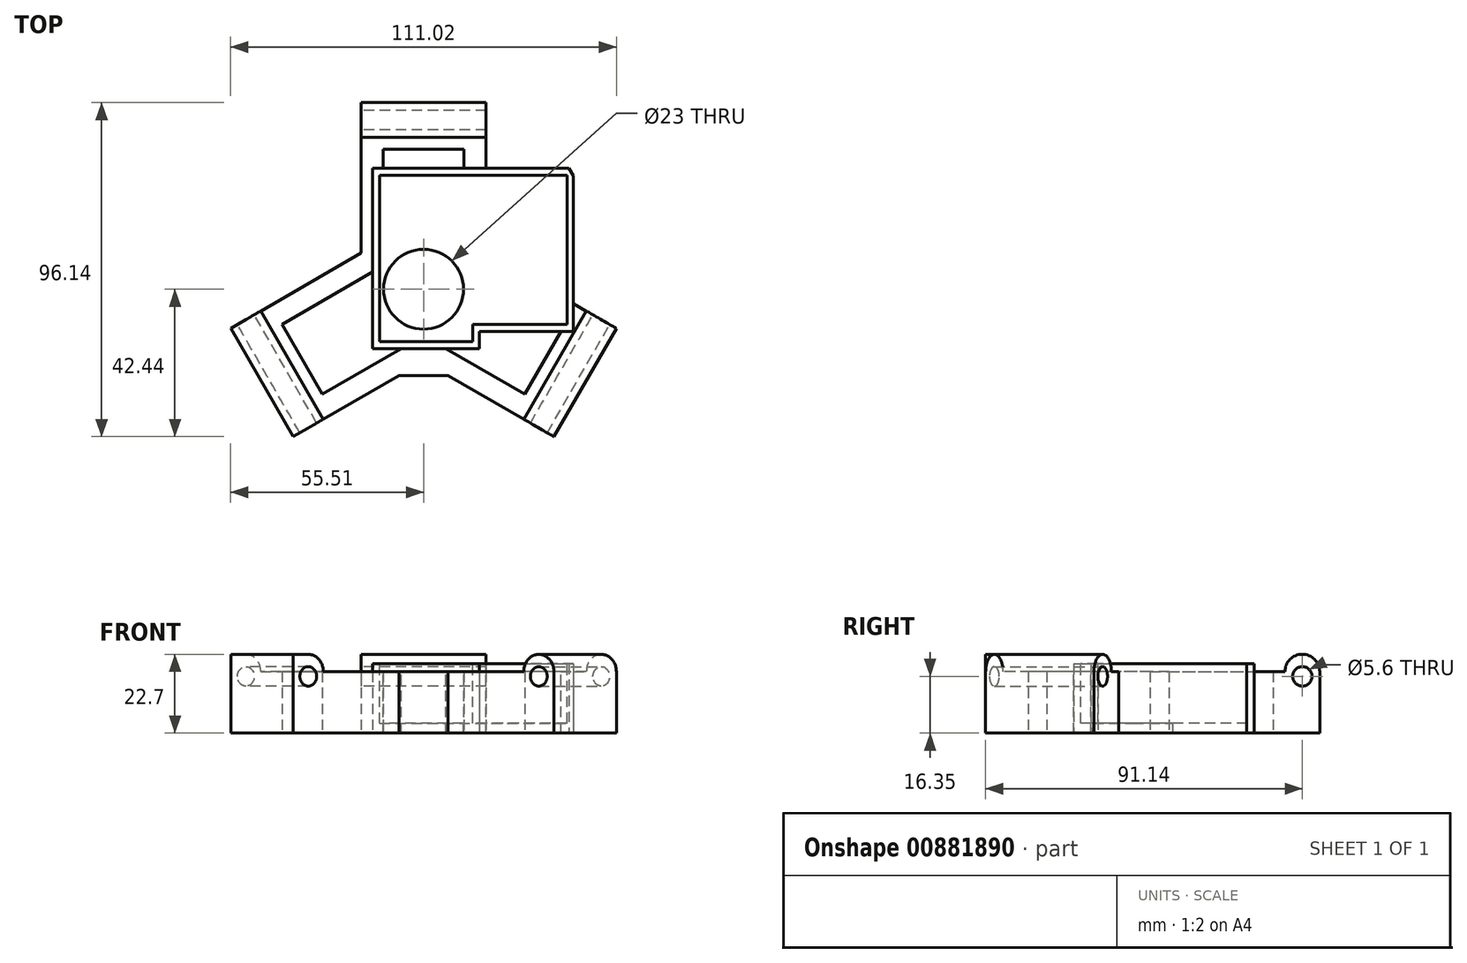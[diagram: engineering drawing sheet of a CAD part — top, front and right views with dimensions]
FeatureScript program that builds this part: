
annotation { "Feature Type Name" : "Feature", "Feature Type Description" : "" }
export const myFeature = defineFeature(function(context is Context, id is Id, definition is map)
    precondition{}
    {
        {
            var Q0;
            Q0=qCreatedBy(makeId("Top.planeOp"),FACE);
            var sketch = newSketch(context, id + "F0", { "sketchPlane" : qUnion([Q0])});
            skCircle(sketch, "E0", {"center": v(0, 0) * mm, "radius": 11.5 * mm});
            skSolve(sketch);
        }
        {
            var Q0;
            Q0=qSketchRegion(id+"F0",true);
            extrude(context, id + "F1", {"entities" : qUnion([Q0]), "depth" : 30.5 * mm, "offsetDistance" : 25 * mm});
        }
        {
            var Q0;
            Q0=makeQuery(id+"F1.opExtrude","CAP_FACE",FACE,{"disambiguationData":[OSD([sQuery(id+"F0.wireOp",EDGE,"E0")])],"isStart":false});
            var sketch = newSketch(context, id + "F2", { "sketchPlane" : qUnion([Q0])});
            skLineSegment(sketch, "E1.bottom", {"start": v(-12.7, 32.85) * mm, "end": v(14.1, 32.85) * mm});
            skLineSegment(sketch, "E1.top", {"start": v(-12.7, -15.1) * mm, "end": v(14.1, -15.1) * mm});
            skLineSegment(sketch, "E1.left", {"start": v(-12.7, 32.85) * mm, "end": v(-12.7, -15.1) * mm});
            skLineSegment(sketch, "E1.right", {"start": v(14.1, 32.85) * mm, "end": v(14.1, -15.1) * mm});
            skSolve(sketch);
        }
        {
            var Q0;
            Q0=qSketchRegion(id+"F2",true);
            extrude(context, id + "F3", {"entities" : qUnion([Q0]), "operationType" : NewBodyOperationType.ADD, "depth" : 44.2 * mm, "offsetDistance" : 25 * mm});
        }
        {
            var Q0;
            Q0=makeQuery(id+"F3.opExtrude","SWEPT_FACE",FACE,{"disambiguationData":[OSD([sQuery(id+"F2.wireOp",EDGE,"E1.right")])]});
            var sketch = newSketch(context, id + "F4", { "sketchPlane" : qUnion([Q0])});
            skLineSegment(sketch, "E2.bottom", {"start": v(32.85, 30.5) * mm, "end": v(-9.15, 30.5) * mm});
            skLineSegment(sketch, "E2.top", {"start": v(32.85, 72.5) * mm, "end": v(-9.15, 72.5) * mm});
            skLineSegment(sketch, "E2.left", {"start": v(32.85, 30.5) * mm, "end": v(32.85, 72.5) * mm});
            skLineSegment(sketch, "E2.right", {"start": v(-9.15, 30.5) * mm, "end": v(-9.15, 72.5) * mm});
            skSolve(sketch);
        }
        {
            var Q0;
            Q0=qSketchRegion(id+"F4",true);
            extrude(context, id + "F5", {"entities" : qUnion([Q0]), "operationType" : NewBodyOperationType.ADD, "depth" : 27.2 * mm, "offsetDistance" : 25 * mm});
        }
        {
            var Q0;
            Q0=qCreatedBy(makeId("Top.planeOp"),FACE);
            var sketch = newSketch(context, id + "F6", { "sketchPlane" : qUnion([Q0])});
            skPoint(sketch, "E3", {"position": v(41.8, 0) * mm});
            skPoint(sketch, "E4", {"position": v(-41.8, 0) * mm});
            skPoint(sketch, "E5", {"position": v(0, 0) * mm});
            skPoint(sketch, "E6", {"position": v(0, -35) * mm});
            skPoint(sketch, "E7", {"position": v(0, 35) * mm});
            skPoint(sketch, "E8", {"position": v(-13, -35) * mm});
            skPoint(sketch, "E9", {"position": v(13, -35) * mm});
            skPoint(sketch, "E10", {"position": v(-13, 35) * mm});
            skPoint(sketch, "E11", {"position": v(13, 35) * mm});
            skLineSegment(sketch, "E12", {"start": v(13, 35) * mm, "end": v(41.8, 35) * mm});
            skLineSegment(sketch, "E13", {"start": v(41.8, 35) * mm, "end": v(41.8, 0) * mm});
            skLineSegment(sketch, "E14", {"start": v(41.8, -35) * mm, "end": v(-41.8, -35) * mm});
            skLineSegment(sketch, "E15", {"start": v(-41.8, 35) * mm, "end": v(-41.8, -35) * mm});
            skLineSegment(sketch, "E16", {"start": v(-41.8, 35) * mm, "end": v(13, 35) * mm});
            skLineSegment(sketch, "E17", {"start": v(41.8, 0) * mm, "end": v(41.8, -35) * mm});
            skLineSegment(sketch, "E18", {"start": v(0, 0) * mm, "end": v(0, 32.21) * mm});
            skSolve(sketch);
        }
        {
            var Q0;
            Q0=qSketchRegion(id+"F6",true);
            extrude(context, id + "F7", {"entities" : qUnion([Q0]), "depth" : 39 * mm, "offsetDistance" : 25 * mm});
        }
        {
            var Q0;
            Q0=makeQuery(id+"F3.opExtrude","CAP_FACE",FACE,{"disambiguationData":[OSD([sQuery(id+"F2.wireOp",EDGE,"E1.bottom"),sQuery(id+"F2.wireOp",EDGE,"E1.top"),sQuery(id+"F2.wireOp",EDGE,"E1.left"),sQuery(id+"F2.wireOp",EDGE,"E1.right")])],"isStart":false});
            var Q1;
            Q1=makeQuery(id+"F5.opExtrude","SWEPT_FACE",FACE,{"disambiguationData":[OSD([sQuery(id+"F4.wireOp",EDGE,"E2.top")])]});
            extrude(context, id + "F8", {"entities" : qUnion([Q0, Q1]), "operationType" : NewBodyOperationType.REMOVE, "oppositeDirection" : true, "depth" : 44.8 * mm, "offsetDistance" : 25 * mm});
        }
        {
            var Q0;
            Q0=makeQuery(id+"F8.boolean.opBoolean","COPY",FACE,{"disambiguationData":[TD([makeQuery(id+"F1.opExtrude","SWEPT_FACE",FACE,{"disambiguationData":[OSD([sQuery(id+"F0.wireOp",EDGE,"E0")])]})])],"derivedFrom":makeQuery(id+"F8.opExtrude","CAP_FACE",FACE,{"disambiguationData":[OSD([sQuery(id+"F2.wireOp",EDGE,"E1.bottom"),sQuery(id+"F2.wireOp",EDGE,"E1.top"),sQuery(id+"F2.wireOp",EDGE,"E1.left"),sQuery(id+"F2.wireOp",EDGE,"E1.right")])],"isStart":false})});
            extrude(context, id + "F9", {"entities" : qUnion([Q0]), "operationType" : NewBodyOperationType.REMOVE, "oppositeDirection" : true, "depth" : 49.1 * mm, "offsetDistance" : 25 * mm});
        }
        {
            var Q0;
            Q0=makeQuery(id+"F7.opExtrude","CAP_FACE",FACE,{"disambiguationData":[OSD([sQuery(id+"F6.wireOp",EDGE,"E12"),sQuery(id+"F6.wireOp",EDGE,"E13"),sQuery(id+"F6.wireOp",EDGE,"E14"),sQuery(id+"F6.wireOp",EDGE,"E15"),sQuery(id+"F6.wireOp",EDGE,"E16"),sQuery(id+"F6.wireOp",EDGE,"E17")])],"isStart":true});
            extrude(context, id + "F10", {"entities" : qUnion([Q0]), "operationType" : NewBodyOperationType.REMOVE, "oppositeDirection" : true, "depth" : 25 * mm, "offsetDistance" : 25 * mm});
        }
        {
            var Q0;
            Q0=makeQuery(id+"F8.boolean.opBoolean","COPY",FACE,{"derivedFrom":makeQuery(id+"F8.opExtrude","CAP_FACE",FACE,{"disambiguationData":[OSD([sQuery(id+"F4.wireOp",EDGE,"E2.top")])],"isStart":false})});
            extrude(context, id + "F11", {"entities" : qUnion([Q0]), "operationType" : NewBodyOperationType.ADD, "depth" : 2.2 * mm, "offsetDistance" : 25 * mm});
        }
        {
            var Q0;
            Q0=makeQuery(id+"F8.boolean.opBoolean","COPY",FACE,{"derivedFrom":makeQuery(id+"F8.opExtrude","SWEPT_FACE",FACE,{"disambiguationData":[OSD([sQuery(id+"F2.wireOp",EDGE,"E1.left")])]})});
            extrude(context, id + "F12", {"entities" : qUnion([Q0]), "operationType" : NewBodyOperationType.REMOVE, "oppositeDirection" : true, "depth" : 2 * mm, "offsetDistance" : 25 * mm});
        }
        {
            var Q0;
            Q0=makeQuery(id+"F7.opExtrude","CAP_FACE",FACE,{"disambiguationData":[OSD([sQuery(id+"F6.wireOp",EDGE,"E12"),sQuery(id+"F6.wireOp",EDGE,"E13"),sQuery(id+"F6.wireOp",EDGE,"E14"),sQuery(id+"F6.wireOp",EDGE,"E15"),sQuery(id+"F6.wireOp",EDGE,"E16"),sQuery(id+"F6.wireOp",EDGE,"E17")])],"isStart":false});
            var sketch = newSketch(context, id + "F13", { "sketchPlane" : qUnion([Q0])});
            skCircle(sketch, "E19.cCircle", {"center": v(0, 0) * mm, "radius": 53.7 * mm, "construction": true});
            skLineSegment(sketch, "E19.0", {"start": v(31, -53.7) * mm, "end": v(-31, -53.7) * mm});
            skLineSegment(sketch, "E19.1", {"start": v(-31, -53.7) * mm, "end": v(-62, 0) * mm});
            skLineSegment(sketch, "E19.2", {"start": v(-62, 0) * mm, "end": v(-31, 53.7) * mm});
            skLineSegment(sketch, "E19.3", {"start": v(-31, 53.7) * mm, "end": v(31, 53.7) * mm});
            skLineSegment(sketch, "E19.4", {"start": v(31, 53.7) * mm, "end": v(62, 0) * mm});
            skLineSegment(sketch, "E19.5", {"start": v(62, 0) * mm, "end": v(31, -53.7) * mm});
            skPoint(sketch, "E19.0.midPoint", {"position": v(0, -53.7) * mm});
            skPoint(sketch, "E20", {"position": v(-41.8, -35) * mm});
            skPoint(sketch, "E21", {"position": v(41.8, -35) * mm});
            skPoint(sketch, "E22", {"position": v(-41.8, 35) * mm});
            skPoint(sketch, "E23", {"position": v(41.8, 35) * mm});
            skSolve(sketch);
        }
        {
            var Q0;
            {var subQ2=sQuery(id+"F13.wireOp",EDGE,"E19.3");Q0=makeQuery(id+"F13.imprint","IMPRINT",FACE,{"disambiguationData":[TD([[makeQuery(id+"F13.imprint","IMPRINT",EDGE,{"derivedFrom":subQ2}),-1.0]])]});}
            var Q1;
            {var subQ1=makeQuery(id+"F7.opExtrude","CAP_EDGE",EDGE,{"disambiguationData":[OSD([sQuery(id+"F6.wireOp",EDGE,"E15")])],"isStart":false});Q1=makeQuery(id+"F13.imprint","IMPRINT",FACE,{"disambiguationData":[TD([[makeQuery(id+"F13.imprint","IMPRINT",EDGE,{"derivedFrom":subQ1}),-1.0]])]});}
            var Q2;
            {var subQ0=sQuery(id+"F13.wireOp",EDGE,"E19.0");Q2=makeQuery(id+"F13.imprint","IMPRINT",FACE,{"disambiguationData":[TD([[makeQuery(id+"F13.imprint","IMPRINT",EDGE,{"derivedFrom":subQ0}),-1.0]])]});}
            var Q3;
            {var subQ1=makeQuery(id+"F7.opExtrude","CAP_EDGE",EDGE,{"disambiguationData":[OSD([sQuery(id+"F6.wireOp",EDGE,"E13"),sQuery(id+"F6.wireOp",EDGE,"E17")])],"isStart":false});Q3=makeQuery(id+"F13.imprint","IMPRINT",FACE,{"disambiguationData":[TD([[makeQuery(id+"F13.imprint","IMPRINT",EDGE,{"derivedFrom":subQ1}),1.0]])]});}
            extrude(context, id + "F14", {"entities" : qUnion([Q0, Q1, Q2, Q3]), "operationType" : NewBodyOperationType.ADD, "oppositeDirection" : true, "depth" : 14 * mm, "offsetDistance" : 25 * mm});
        }
        {
            var Q0;
            {var subQ0=sQuery(id+"F13.wireOp",EDGE,"E19.5");var subQ1=sQuery(id+"F13.wireOp",EDGE,"E19.4");var subQ2=sQuery(id+"F6.wireOp",EDGE,"E17");var subQ3=sQuery(id+"F6.wireOp",EDGE,"E13");var subQ4=sQuery(id+"F13.wireOp",EDGE,"E19.2");var subQ5=sQuery(id+"F6.wireOp",EDGE,"E16");var subQ6=sQuery(id+"F6.wireOp",EDGE,"E12");var subQ7=sQuery(id+"F13.wireOp",EDGE,"E19.1");var subQ8=sQuery(id+"F6.wireOp",EDGE,"E15");var subQ9=sQuery(id+"F6.wireOp",EDGE,"E14");Q0=makeQuery(id+"F14.boolean.opBoolean","MERGE",FACE,{"derivedFrom":[makeQuery(id+"F7.opExtrude","CAP_FACE",FACE,{"disambiguationData":[OSD([subQ6,subQ3,subQ9,subQ8,subQ5,subQ2])],"isStart":false}),makeQuery(id+"F14.opExtrude","CAP_FACE",FACE,{"disambiguationData":[OSD([subQ9,sQuery(id+"F13.wireOp",EDGE,"E19.0"),subQ7,subQ0])],"isStart":true}),makeQuery(id+"F14.opExtrude","CAP_FACE",FACE,{"disambiguationData":[OSD([subQ8,subQ7,subQ4])],"isStart":true}),makeQuery(id+"F14.opExtrude","CAP_FACE",FACE,{"disambiguationData":[OSD([subQ6,subQ5,subQ4,sQuery(id+"F13.wireOp",EDGE,"E19.3"),subQ1])],"isStart":true}),makeQuery(id+"F14.opExtrude","CAP_FACE",FACE,{"disambiguationData":[OSD([subQ3,subQ2,subQ1,subQ0])],"isStart":true})]});}
            var sketch = newSketch(context, id + "F15", { "sketchPlane" : qUnion([Q0])});
            skPoint(sketch, "E24", {"position": v(-36.78, 43.7) * mm});
            skPoint(sketch, "E25", {"position": v(-62, 0) * mm});
            skPoint(sketch, "E26", {"position": v(-56.23, 10) * mm});
            skPoint(sketch, "E27", {"position": v(-31, -53.7) * mm});
            skPoint(sketch, "E28", {"position": v(-53.35, 5) * mm});
            skPoint(sketch, "E29", {"position": v(62, 0) * mm});
            skPoint(sketch, "E30", {"position": v(31, -53.7) * mm});
            skPoint(sketch, "E31", {"position": v(56.23, 10) * mm});
            skLineSegment(sketch, "E32", {"start": v(62, 0) * mm, "end": v(53.35, 5) * mm});
            skPoint(sketch, "E33", {"position": v(-37.85, -21.85) * mm});
            skPoint(sketch, "E34", {"position": v(-46.5, -26.85) * mm});
            skPoint(sketch, "E35", {"position": v(-28.85, -37.44) * mm});
            skPoint(sketch, "E36", {"position": v(-46.85, -6.26) * mm});
            skLineSegment(sketch, "E37", {"start": v(-46.85, -6.26) * mm, "end": v(-55.5, -11.26) * mm});
            skLineSegment(sketch, "E38", {"start": v(-55.5, -11.26) * mm, "end": v(-46.5, -26.85) * mm});
            skLineSegment(sketch, "E39", {"start": v(-28.85, -37.44) * mm, "end": v(-37.5, -42.44) * mm});
            skLineSegment(sketch, "E40", {"start": v(-37.5, -42.44) * mm, "end": v(-46.5, -26.85) * mm});
            skLineSegment(sketch, "E41", {"start": v(-46.85, -6.26) * mm, "end": v(-28.85, -37.44) * mm});
            skLineSegment(sketch, "E42", {"start": v(-55.5, -11.26) * mm, "end": v(-37.5, -42.44) * mm});
            skPoint(sketch, "E43", {"position": v(0, 43.7) * mm});
            skPoint(sketch, "E44", {"position": v(0, 53.7) * mm});
            skPoint(sketch, "E45", {"position": v(-18, 53.7) * mm});
            skPoint(sketch, "E46", {"position": v(18, 53.7) * mm});
            skLineSegment(sketch, "E47.bottom", {"start": v(-18, 53.7) * mm, "end": v(18, 53.7) * mm});
            skLineSegment(sketch, "E47.top", {"start": v(-18, 43.7) * mm, "end": v(18, 43.7) * mm});
            skLineSegment(sketch, "E47.left", {"start": v(-18, 53.7) * mm, "end": v(-18, 43.7) * mm});
            skLineSegment(sketch, "E47.right", {"start": v(18, 53.7) * mm, "end": v(18, 43.7) * mm});
            skPoint(sketch, "E48", {"position": v(37.85, -21.85) * mm});
            skPoint(sketch, "E49", {"position": v(46.5, -26.85) * mm});
            skPoint(sketch, "E50", {"position": v(28.85, -37.44) * mm});
            skPoint(sketch, "E51", {"position": v(46.85, -6.26) * mm});
            skLineSegment(sketch, "E52", {"start": v(28.85, -37.44) * mm, "end": v(37.5, -42.44) * mm});
            skLineSegment(sketch, "E53", {"start": v(37.5, -42.44) * mm, "end": v(55.5, -11.26) * mm});
            skLineSegment(sketch, "E54", {"start": v(55.5, -11.26) * mm, "end": v(46.85, -6.26) * mm});
            skLineSegment(sketch, "E55", {"start": v(46.85, -6.26) * mm, "end": v(28.85, -37.44) * mm});
            skSolve(sketch);
        }
        {
            var Q0;
            Q0=makeQuery(id+"F15.imprint","IMPRINT",FACE,{"disambiguationData":[TD([[makeQuery(id+"F15.imprint","IMPRINT",EDGE,{"derivedFrom":sQuery(id+"F15.wireOp",EDGE,"E37")}),1.0]])]});
            var Q1;
            Q1=makeQuery(id+"F15.imprint","IMPRINT",FACE,{"disambiguationData":[TD([[makeQuery(id+"F15.imprint","IMPRINT",EDGE,{"derivedFrom":sQuery(id+"F15.wireOp",EDGE,"E47.bottom")}),-1.0]])]});
            var Q2;
            Q2=makeQuery(id+"F15.imprint","IMPRINT",FACE,{"disambiguationData":[TD([[makeQuery(id+"F15.imprint","IMPRINT",EDGE,{"derivedFrom":sQuery(id+"F15.wireOp",EDGE,"E52")}),1.0]])]});
            extrude(context, id + "F16", {"entities" : qUnion([Q0, Q1, Q2]), "operationType" : NewBodyOperationType.ADD, "depth" : 12.7 * mm, "offsetDistance" : 25 * mm});
        }
        {
            var Q0;
            Q0=makeQuery(id+"F10.boolean.opBoolean","COPY",FACE,{"derivedFrom":makeQuery(id+"F10.opExtrude","CAP_FACE",FACE,{"disambiguationData":[OSD([sQuery(id+"F6.wireOp",EDGE,"E12"),sQuery(id+"F6.wireOp",EDGE,"E13"),sQuery(id+"F6.wireOp",EDGE,"E14"),sQuery(id+"F6.wireOp",EDGE,"E15"),sQuery(id+"F6.wireOp",EDGE,"E16"),sQuery(id+"F6.wireOp",EDGE,"E17")])],"isStart":false})});
            var Q1;
            Q1=makeQuery(id+"F14.opExtrude","CAP_FACE",FACE,{"disambiguationData":[OSD([sQuery(id+"F6.wireOp",EDGE,"E15"),sQuery(id+"F13.wireOp",EDGE,"E19.1"),sQuery(id+"F13.wireOp",EDGE,"E19.2")])],"isStart":false});
            var Q2;
            Q2=makeQuery(id+"F14.opExtrude","CAP_FACE",FACE,{"disambiguationData":[OSD([sQuery(id+"F6.wireOp",EDGE,"E14"),sQuery(id+"F13.wireOp",EDGE,"E19.0"),sQuery(id+"F13.wireOp",EDGE,"E19.1"),sQuery(id+"F13.wireOp",EDGE,"E19.5")])],"isStart":false});
            var Q3;
            Q3=makeQuery(id+"F14.opExtrude","CAP_FACE",FACE,{"disambiguationData":[OSD([sQuery(id+"F6.wireOp",EDGE,"E13"),sQuery(id+"F6.wireOp",EDGE,"E17"),sQuery(id+"F13.wireOp",EDGE,"E19.4"),sQuery(id+"F13.wireOp",EDGE,"E19.5")])],"isStart":false});
            var Q4;
            Q4=makeQuery(id+"F14.opExtrude","CAP_FACE",FACE,{"disambiguationData":[OSD([sQuery(id+"F6.wireOp",EDGE,"E12"),sQuery(id+"F6.wireOp",EDGE,"E16"),sQuery(id+"F13.wireOp",EDGE,"E19.2"),sQuery(id+"F13.wireOp",EDGE,"E19.3"),sQuery(id+"F13.wireOp",EDGE,"E19.4")])],"isStart":false});
            extrude(context, id + "F17", {"entities" : qUnion([Q0, Q1, Q2, Q3, Q4]), "operationType" : NewBodyOperationType.REMOVE, "oppositeDirection" : true, "depth" : 4 * mm, "offsetDistance" : 25 * mm});
        }
        {
            var Q0;
            Q0=makeQuery(id+"F8.boolean.opBoolean","COPY",FACE,{"derivedFrom":makeQuery(id+"F8.opExtrude","SWEPT_FACE",FACE,{"disambiguationData":[OSD([sQuery(id+"F4.wireOp",EDGE,"E2.top"),sQuery(id+"F4.wireOp",EDGE,"E2.right")])]})});
            extrude(context, id + "F18", {"entities" : qUnion([Q0]), "operationType" : NewBodyOperationType.REMOVE, "oppositeDirection" : true, "depth" : 2 * mm, "offsetDistance" : 25 * mm});
        }
        {
            var Q0;
            {var subQ0=sQuery(id+"F2.wireOp",EDGE,"E1.top");Q0=makeQuery(id+"F12.boolean.opBoolean","MERGE",FACE,{"derivedFrom":[makeQuery(id+"F8.boolean.opBoolean","COPY",FACE,{"derivedFrom":makeQuery(id+"F8.opExtrude","SWEPT_FACE",FACE,{"disambiguationData":[OSD([subQ0])]})})],"fromTools":[makeQuery(id+"F12.opExtrude","SWEPT_FACE",FACE,{"disambiguationData":[OSD([subQ0,sQuery(id+"F2.wireOp",EDGE,"E1.left")])]})]});}
            extrude(context, id + "F19", {"entities" : qUnion([Q0]), "operationType" : NewBodyOperationType.REMOVE, "oppositeDirection" : true, "depth" : 2 * mm, "offsetDistance" : 25 * mm});
        }
        {
            var Q0;
            Q0=makeQuery(id+"F14.opExtrude","SWEPT_EDGE",EDGE,{"disambiguationData":[OSD([sQuery(id+"F13.wireOp",EDGE,"E19.4"),sQuery(id+"F13.wireOp",EDGE,"E19.5")])]});
            var Q1;
            Q1=makeQuery(id+"F14.opExtrude","SWEPT_EDGE",EDGE,{"disambiguationData":[OSD([sQuery(id+"F13.wireOp",EDGE,"E19.3"),sQuery(id+"F13.wireOp",EDGE,"E19.4")])]});
            var Q2;
            Q2=makeQuery(id+"F14.opExtrude","SWEPT_EDGE",EDGE,{"disambiguationData":[OSD([sQuery(id+"F13.wireOp",EDGE,"E19.0"),sQuery(id+"F13.wireOp",EDGE,"E19.5")])]});
            var Q3;
            Q3=makeQuery(id+"F14.opExtrude","SWEPT_EDGE",EDGE,{"disambiguationData":[OSD([sQuery(id+"F13.wireOp",EDGE,"E19.0"),sQuery(id+"F13.wireOp",EDGE,"E19.1")])]});
            var Q4;
            Q4=makeQuery(id+"F14.opExtrude","SWEPT_EDGE",EDGE,{"disambiguationData":[OSD([sQuery(id+"F13.wireOp",EDGE,"E19.2"),sQuery(id+"F13.wireOp",EDGE,"E19.3")])]});
            var Q5;
            Q5=makeQuery(id+"F14.opExtrude","SWEPT_EDGE",EDGE,{"disambiguationData":[OSD([sQuery(id+"F13.wireOp",EDGE,"E19.1"),sQuery(id+"F13.wireOp",EDGE,"E19.2")])]});
            chamfer(context, id + "F20", {"entities" : qUnion([Q0, Q1, Q2, Q3, Q4, Q5]), "width" : 13 * mm, "tangentPropagation" : true});
        }
        {
            var Q0;
            Q0=makeQuery(id+"F16.opExtrude","CAP_EDGE",EDGE,{"disambiguationData":[OSD([sQuery(id+"F15.wireOp",EDGE,"E53")])],"isStart":false});
            var Q1;
            Q1=makeQuery(id+"F16.opExtrude","CAP_EDGE",EDGE,{"disambiguationData":[OSD([sQuery(id+"F15.wireOp",EDGE,"E55")])],"isStart":false});
            var Q2;
            Q2=makeQuery(id+"F16.opExtrude","CAP_EDGE",EDGE,{"disambiguationData":[OSD([sQuery(id+"F15.wireOp",EDGE,"E47.bottom")])],"isStart":false});
            var Q3;
            Q3=makeQuery(id+"F16.opExtrude","CAP_EDGE",EDGE,{"disambiguationData":[OSD([sQuery(id+"F15.wireOp",EDGE,"E47.top")])],"isStart":false});
            var Q4;
            Q4=makeQuery(id+"F16.opExtrude","CAP_EDGE",EDGE,{"disambiguationData":[OSD([sQuery(id+"F15.wireOp",EDGE,"E41")])],"isStart":false});
            var Q5;
            Q5=makeQuery(id+"F16.opExtrude","CAP_EDGE",EDGE,{"disambiguationData":[OSD([sQuery(id+"F15.wireOp",EDGE,"E42")])],"isStart":false});
            fillet(context, id + "F21", {"entities" : qUnion([Q0, Q1, Q2, Q3, Q4, Q5]), "radius" : 5 * mm, "tangentPropagation" : true, "allowEdgeOverflow" : false});
        }
        {
            var Q0;
            Q0=makeQuery(id+"F16.opExtrude","SWEPT_FACE",FACE,{"disambiguationData":[OSD([sQuery(id+"F15.wireOp",EDGE,"E54")])]});
            var sketch = newSketch(context, id + "F22", { "sketchPlane" : qUnion([Q0])});
            skPoint(sketch, "E56", {"position": v(-48.7, 51.7) * mm});
            skPoint(sketch, "E57", {"position": v(-48.7, 39) * mm});
            skPoint(sketch, "E58", {"position": v(-48.7, 45.35) * mm});
            skCircle(sketch, "E59", {"center": v(-48.7, 45.35) * mm, "radius": 2.8 * mm});
            skSolve(sketch);
        }
        {
            var Q0;
            Q0=qSketchRegion(id+"F22",true);
            extrude(context, id + "F23", {"entities" : qUnion([Q0]), "operationType" : NewBodyOperationType.REMOVE, "oppositeDirection" : true, "depth" : 54.7 * mm, "offsetDistance" : 25 * mm});
        }
        {
            var Q0;
            Q0=makeQuery(id+"F16.opExtrude","SWEPT_FACE",FACE,{"disambiguationData":[OSD([sQuery(id+"F15.wireOp",EDGE,"E47.left")])]});
            var sketch = newSketch(context, id + "F24", { "sketchPlane" : qUnion([Q0])});
            skPoint(sketch, "E60", {"position": v(-48.7, 51.7) * mm});
            skPoint(sketch, "E61", {"position": v(-48.7, 39) * mm});
            skPoint(sketch, "E62", {"position": v(-48.7, 45.35) * mm});
            skCircle(sketch, "E63", {"center": v(-48.7, 45.35) * mm, "radius": 2.8 * mm});
            skSolve(sketch);
        }
        {
            var Q0;
            Q0=qSketchRegion(id+"F24",true);
            extrude(context, id + "F25", {"entities" : qUnion([Q0]), "operationType" : NewBodyOperationType.REMOVE, "oppositeDirection" : true, "depth" : 55.8 * mm, "offsetDistance" : 25 * mm});
        }
        {
            var Q0;
            Q0=makeQuery(id+"F16.opExtrude","SWEPT_FACE",FACE,{"disambiguationData":[OSD([sQuery(id+"F15.wireOp",EDGE,"E37")])]});
            var sketch = newSketch(context, id + "F26", { "sketchPlane" : qUnion([Q0])});
            skPoint(sketch, "E64", {"position": v(48.7, 51.7) * mm});
            skPoint(sketch, "E65", {"position": v(48.7, 39) * mm});
            skPoint(sketch, "E66", {"position": v(48.7, 45.35) * mm});
            skCircle(sketch, "E67", {"center": v(48.7, 45.35) * mm, "radius": 2.8 * mm});
            skSolve(sketch);
        }
        {
            var Q0;
            Q0=qSketchRegion(id+"F26",true);
            extrude(context, id + "F27", {"entities" : qUnion([Q0]), "operationType" : NewBodyOperationType.REMOVE, "oppositeDirection" : true, "depth" : 44.4 * mm, "offsetDistance" : 25 * mm});
        }
        {
            var Q0;
            {var subQ37=sQuery(id+"F15.wireOp",EDGE,"E37");Q0=makeQuery(id+"F15.imprint","IMPRINT",FACE,{"disambiguationData":[TD([[makeQuery(id+"F15.imprint","IMPRINT",EDGE,{"derivedFrom":subQ37}),-1.0]])]});}
            extrude(context, id + "F28", {"entities" : qUnion([Q0]), "operationType" : NewBodyOperationType.REMOVE, "oppositeDirection" : true, "depth" : 5 * mm, "offsetDistance" : 25 * mm});
        }
        {
            var Q0;
            Q0=makeQuery(id+"F18.boolean.opBoolean","COPY",FACE,{"derivedFrom":makeQuery(id+"F18.opExtrude","CAP_FACE",FACE,{"disambiguationData":[OSD([sQuery(id+"F4.wireOp",EDGE,"E2.top"),sQuery(id+"F4.wireOp",EDGE,"E2.right")])],"isStart":false})});
            extrude(context, id + "F29", {"entities" : qUnion([Q0]), "operationType" : NewBodyOperationType.ADD, "depth" : 1 * mm, "offsetDistance" : 25 * mm});
        }
        {
            var Q0;
            Q0=makeQuery(id+"F19.boolean.opBoolean","COPY",FACE,{"derivedFrom":makeQuery(id+"F19.opExtrude","CAP_FACE",FACE,{"disambiguationData":[OSD([sQuery(id+"F2.wireOp",EDGE,"E1.top"),sQuery(id+"F2.wireOp",EDGE,"E1.left")])],"isStart":false})});
            extrude(context, id + "F30", {"entities" : qUnion([Q0]), "operationType" : NewBodyOperationType.ADD, "depth" : 2 * mm, "offsetDistance" : 25 * mm});
        }
        {
            var Q0;
            {var subQ0=sQuery(id+"F2.wireOp",EDGE,"E1.left");var subQ1=sQuery(id+"F2.wireOp",EDGE,"E1.top");Q0=makeQuery(id+"F19.boolean.opBoolean","MERGE",FACE,{"derivedFrom":[makeQuery(id+"F12.boolean.opBoolean","COPY",FACE,{"derivedFrom":makeQuery(id+"F12.opExtrude","CAP_FACE",FACE,{"disambiguationData":[OSD([subQ0])],"isStart":false})})],"fromTools":[makeQuery(id+"F19.opExtrude","SWEPT_FACE",FACE,{"disambiguationData":[OSD([subQ1,subQ0]),TDD([makeQuery(id+"F12.boolean.opBoolean","COPY",EDGE,{"derivedFrom":makeQuery(id+"F12.opExtrude","CAP_EDGE",EDGE,{"disambiguationData":[OSD([subQ1,subQ0])],"isStart":false})})])]})]});}
            extrude(context, id + "F31", {"entities" : qUnion([Q0]), "operationType" : NewBodyOperationType.ADD, "depth" : 2 * mm, "offsetDistance" : 25 * mm});
        }
        {
            var Q0;
            {var subQ0=sQuery(id+"F15.wireOp",EDGE,"E55");var subQ1=sQuery(id+"F15.wireOp",EDGE,"E54");var subQ2=sQuery(id+"F15.wireOp",EDGE,"E52");var subQ3=sQuery(id+"F15.wireOp",EDGE,"E47.right");var subQ4=sQuery(id+"F15.wireOp",EDGE,"E47.left");var subQ5=sQuery(id+"F15.wireOp",EDGE,"E47.top");var subQ6=sQuery(id+"F15.wireOp",EDGE,"E41");var subQ7=sQuery(id+"F15.wireOp",EDGE,"E39");var subQ8=sQuery(id+"F15.wireOp",EDGE,"E37");var subQ9=sQuery(id+"F13.wireOp",EDGE,"E19.5");var subQ10=sQuery(id+"F13.wireOp",EDGE,"E19.4");var subQ11=sQuery(id+"F13.wireOp",EDGE,"E19.3");var subQ12=sQuery(id+"F13.wireOp",EDGE,"E19.2");var subQ13=sQuery(id+"F13.wireOp",EDGE,"E19.1");var subQ14=sQuery(id+"F13.wireOp",EDGE,"E19.0");var subQ15=sQuery(id+"F6.wireOp",EDGE,"E17");var subQ16=sQuery(id+"F6.wireOp",EDGE,"E16");var subQ17=sQuery(id+"F6.wireOp",EDGE,"E15");var subQ18=sQuery(id+"F6.wireOp",EDGE,"E14");var subQ19=sQuery(id+"F6.wireOp",EDGE,"E13");var subQ20=sQuery(id+"F6.wireOp",EDGE,"E12");var subQ21=sQuery(id+"F4.wireOp",EDGE,"E2.right");var subQ22=sQuery(id+"F4.wireOp",EDGE,"E2.left");var subQ23=sQuery(id+"F4.wireOp",EDGE,"E2.top");var subQ24=sQuery(id+"F2.wireOp",EDGE,"E1.right");var subQ25=sQuery(id+"F2.wireOp",EDGE,"E1.left");var subQ26=sQuery(id+"F2.wireOp",EDGE,"E1.top");var subQ27=sQuery(id+"F2.wireOp",EDGE,"E1.bottom");Q0=makeQuery(id+"F31.boolean.opBoolean","MERGE",FACE,{"derivedFrom":[makeQuery(id+"F30.boolean.opBoolean","MERGE",FACE,{"derivedFrom":[makeQuery(id+"F29.boolean.opBoolean","MERGE",FACE,{"derivedFrom":[makeQuery(id+"F28.boolean.opBoolean","COPY",FACE,{"derivedFrom":makeQuery(id+"F28.opExtrude","CAP_FACE",FACE,{"disambiguationData":[OSD([subQ27,subQ26,subQ25,subQ24,subQ23,subQ22,subQ21,subQ20,subQ19,subQ18,subQ17,subQ16,subQ15,subQ14,subQ13,subQ12,subQ11,subQ10,subQ9,subQ8,subQ7,subQ6,subQ5,subQ4,subQ3,subQ2,subQ1,subQ0])],"isStart":false})}),makeQuery(id+"F29.opExtrude","SWEPT_FACE",FACE,{"disambiguationData":[OSD([subQ27,subQ26,subQ25,subQ24,subQ23,subQ22,subQ21,subQ20,subQ19,subQ18,subQ17,subQ16,subQ15,subQ14,subQ13,subQ12,subQ11,subQ10,subQ9,subQ8,subQ7,subQ6,subQ5,subQ4,subQ3,subQ2,subQ1,subQ0])]})]}),makeQuery(id+"F30.opExtrude","SWEPT_FACE",FACE,{"disambiguationData":[OSD([subQ27,subQ26,subQ25,subQ24,subQ23,subQ22,subQ21,subQ20,subQ19,subQ18,subQ17,subQ16,subQ15,subQ14,subQ13,subQ12,subQ11,subQ10,subQ9,subQ8,subQ7,subQ6,subQ5,subQ4,subQ3,subQ2,subQ1,subQ0])]})]}),makeQuery(id+"F31.opExtrude","SWEPT_FACE",FACE,{"disambiguationData":[OSD([subQ27,subQ26,subQ25,subQ24,subQ23,subQ22,subQ21,subQ20,subQ19,subQ18,subQ17,subQ16,subQ15,subQ14,subQ13,subQ12,subQ11,subQ10,subQ9,subQ8,subQ7,subQ6,subQ5,subQ4,subQ3,subQ2,subQ1,subQ0])]})]});}
            var sketch = newSketch(context, id + "F32", { "sketchPlane" : qUnion([Q0])});
            skPoint(sketch, "E68", {"position": v(-12.7, 8.88) * mm});
            skPoint(sketch, "E69", {"position": v(-14.7, 8.88) * mm});
            skPoint(sketch, "E70", {"position": v(0.7, -15.1) * mm});
            skPoint(sketch, "E71", {"position": v(0.7, -17.1) * mm});
            skPoint(sketch, "E72", {"position": v(27.7, -10.15) * mm});
            skPoint(sketch, "E73", {"position": v(27.7, -12.15) * mm});
            skPoint(sketch, "E74", {"position": v(41.3, 11.35) * mm});
            skPoint(sketch, "E75", {"position": v(43.16, 11.35) * mm});
            skPoint(sketch, "E76", {"position": v(14.1, 32.85) * mm});
            skPoint(sketch, "E77", {"position": v(14.1, 34.85) * mm});
            skPoint(sketch, "E78", {"position": v(-12.7, 32.85) * mm});
            skPoint(sketch, "E79", {"position": v(-12.7, -15.1) * mm});
            skPoint(sketch, "E80", {"position": v(14.1, -15.1) * mm});
            skPoint(sketch, "E81", {"position": v(41.3, -10.15) * mm});
            skPoint(sketch, "E82", {"position": v(41.3, 32.85) * mm});
            skLineSegment(sketch, "E83", {"start": v(-14.7, 8.88) * mm, "end": v(-14.7, 34.85) * mm});
            skLineSegment(sketch, "E84", {"start": v(-14.7, 34.85) * mm, "end": v(41.89, 34.85) * mm});
            skLineSegment(sketch, "E85", {"start": v(-14.7, 8.88) * mm, "end": v(-14.7, -17.1) * mm});
            skPoint(sketch, "E86", {"position": v(16.1, -12.15) * mm});
            skLineSegment(sketch, "E87", {"start": v(-14.7, -17.1) * mm, "end": v(16.1, -17.1) * mm});
            skLineSegment(sketch, "E88", {"start": v(16.1, -17.1) * mm, "end": v(16.1, -12.15) * mm});
            skLineSegment(sketch, "E89", {"start": v(43.16, -12.15) * mm, "end": v(16.1, -12.15) * mm});
            skLineSegment(sketch, "E90", {"start": v(43.16, -12.15) * mm, "end": v(43.16, 32.64) * mm});
            skLineSegment(sketch, "E91", {"start": v(43.16, 32.64) * mm, "end": v(41.89, 34.85) * mm});
            skLineSegment(sketch, "E92", {"start": v(-12.7, 32.85) * mm, "end": v(-12.7, -15.1) * mm});
            skLineSegment(sketch, "E93", {"start": v(14.1, -15.1) * mm, "end": v(14.1, -10.15) * mm});
            skLineSegment(sketch, "E94", {"start": v(14.1, -10.15) * mm, "end": v(41.3, -10.15) * mm});
            skLineSegment(sketch, "E95", {"start": v(41.3, 32.85) * mm, "end": v(41.3, -10.15) * mm});
            skLineSegment(sketch, "E96", {"start": v(41.3, 32.85) * mm, "end": v(-12.7, 32.85) * mm});
            skSolve(sketch);
        }
        {
            var Q0;
            Q0=makeQuery(id+"F32.imprint","IMPRINT",FACE,{"disambiguationData":[TD([[makeQuery(id+"F32.imprint","IMPRINT",EDGE,{"derivedFrom":sQuery(id+"F32.wireOp",EDGE,"E83")}),-1.0]])]});
            extrude(context, id + "F33", {"entities" : qUnion([Q0]), "operationType" : NewBodyOperationType.ADD, "depth" : 15 * mm, "offsetDistance" : 25 * mm});
        }
        {
            var Q0;
            {var subQ0=sQuery(id+"F2.wireOp",EDGE,"E1.left");var subQ1=sQuery(id+"F2.wireOp",EDGE,"E1.top");var subQ2=sQuery(id+"F4.wireOp",EDGE,"E2.right");var subQ3=sQuery(id+"F4.wireOp",EDGE,"E2.top");var subQ4=sQuery(id+"F2.wireOp",EDGE,"E1.right");var subQ5=sQuery(id+"F2.wireOp",EDGE,"E1.bottom");Q0=makeQuery(id+"F19.boolean.opBoolean","MERGE",FACE,{"derivedFrom":[makeQuery(id+"F18.boolean.opBoolean","MERGE",FACE,{"derivedFrom":[makeQuery(id+"F12.boolean.opBoolean","MERGE",FACE,{"derivedFrom":[makeQuery(id+"F11.boolean.opBoolean","MERGE",FACE,{"derivedFrom":[makeQuery(id+"F8.boolean.opBoolean","COPY",FACE,{"disambiguationData":[TD([makeQuery(id+"F8.opExtrude","SWEPT_FACE",FACE,{"disambiguationData":[OSD([subQ5])]})])],"derivedFrom":makeQuery(id+"F8.opExtrude","CAP_FACE",FACE,{"disambiguationData":[OSD([subQ5,subQ1,subQ0,subQ4])],"isStart":false})}),makeQuery(id+"F11.opExtrude","CAP_FACE",FACE,{"disambiguationData":[OSD([subQ3])],"isStart":false})]})],"fromTools":[makeQuery(id+"F12.opExtrude","SWEPT_FACE",FACE,{"disambiguationData":[OSD([subQ0])]})]})],"fromTools":[makeQuery(id+"F18.opExtrude","SWEPT_FACE",FACE,{"disambiguationData":[OSD([subQ3,subQ2]),TDD([makeQuery(id+"F11.opExtrude","CAP_EDGE",EDGE,{"disambiguationData":[OSD([subQ3,subQ2])],"isStart":false})])]})]})],"fromTools":[makeQuery(id+"F19.opExtrude","SWEPT_FACE",FACE,{"disambiguationData":[OSD([subQ1,subQ0]),TDD([makeQuery(id+"F12.boolean.opBoolean","MERGE",EDGE,{"derivedFrom":[makeQuery(id+"F8.boolean.opBoolean","COPY",EDGE,{"derivedFrom":makeQuery(id+"F8.opExtrude","CAP_EDGE",EDGE,{"disambiguationData":[OSD([subQ1])],"isStart":false})})],"fromTools":[makeQuery(id+"F12.opExtrude","SWEPT_EDGE",EDGE,{"disambiguationData":[OSD([subQ1,subQ0])]})]})])]})]});}
            extrude(context, id + "F34", {"entities" : qUnion([Q0]), "operationType" : NewBodyOperationType.ADD, "depth" : 2 * mm, "offsetDistance" : 25 * mm});
        }
        {
            var Q0;
            {var subQ0=sQuery(id+"F15.wireOp",EDGE,"E55");var subQ1=sQuery(id+"F15.wireOp",EDGE,"E54");var subQ2=sQuery(id+"F15.wireOp",EDGE,"E52");var subQ3=sQuery(id+"F15.wireOp",EDGE,"E47.right");var subQ4=sQuery(id+"F15.wireOp",EDGE,"E47.left");var subQ5=sQuery(id+"F15.wireOp",EDGE,"E47.top");var subQ6=sQuery(id+"F15.wireOp",EDGE,"E41");var subQ7=sQuery(id+"F15.wireOp",EDGE,"E39");var subQ8=sQuery(id+"F15.wireOp",EDGE,"E37");var subQ9=sQuery(id+"F13.wireOp",EDGE,"E19.5");var subQ10=sQuery(id+"F13.wireOp",EDGE,"E19.4");var subQ11=sQuery(id+"F13.wireOp",EDGE,"E19.3");var subQ12=sQuery(id+"F13.wireOp",EDGE,"E19.2");var subQ13=sQuery(id+"F13.wireOp",EDGE,"E19.1");var subQ14=sQuery(id+"F13.wireOp",EDGE,"E19.0");var subQ15=sQuery(id+"F6.wireOp",EDGE,"E17");var subQ16=sQuery(id+"F6.wireOp",EDGE,"E16");var subQ17=sQuery(id+"F6.wireOp",EDGE,"E15");var subQ18=sQuery(id+"F6.wireOp",EDGE,"E14");var subQ19=sQuery(id+"F6.wireOp",EDGE,"E13");var subQ20=sQuery(id+"F6.wireOp",EDGE,"E12");var subQ21=sQuery(id+"F4.wireOp",EDGE,"E2.right");var subQ22=sQuery(id+"F4.wireOp",EDGE,"E2.left");var subQ23=sQuery(id+"F4.wireOp",EDGE,"E2.top");var subQ24=sQuery(id+"F2.wireOp",EDGE,"E1.right");var subQ25=sQuery(id+"F2.wireOp",EDGE,"E1.left");var subQ26=sQuery(id+"F2.wireOp",EDGE,"E1.top");var subQ27=sQuery(id+"F2.wireOp",EDGE,"E1.bottom");Q0=makeQuery(id+"F31.boolean.opBoolean","MERGE",FACE,{"derivedFrom":[makeQuery(id+"F30.boolean.opBoolean","MERGE",FACE,{"derivedFrom":[makeQuery(id+"F29.boolean.opBoolean","MERGE",FACE,{"derivedFrom":[makeQuery(id+"F28.boolean.opBoolean","COPY",FACE,{"derivedFrom":makeQuery(id+"F28.opExtrude","CAP_FACE",FACE,{"disambiguationData":[OSD([subQ27,subQ26,subQ25,subQ24,subQ23,subQ22,subQ21,subQ20,subQ19,subQ18,subQ17,subQ16,subQ15,subQ14,subQ13,subQ12,subQ11,subQ10,subQ9,subQ8,subQ7,subQ6,subQ5,subQ4,subQ3,subQ2,subQ1,subQ0])],"isStart":false})}),makeQuery(id+"F29.opExtrude","SWEPT_FACE",FACE,{"disambiguationData":[OSD([subQ27,subQ26,subQ25,subQ24,subQ23,subQ22,subQ21,subQ20,subQ19,subQ18,subQ17,subQ16,subQ15,subQ14,subQ13,subQ12,subQ11,subQ10,subQ9,subQ8,subQ7,subQ6,subQ5,subQ4,subQ3,subQ2,subQ1,subQ0])]})]}),makeQuery(id+"F30.opExtrude","SWEPT_FACE",FACE,{"disambiguationData":[OSD([subQ27,subQ26,subQ25,subQ24,subQ23,subQ22,subQ21,subQ20,subQ19,subQ18,subQ17,subQ16,subQ15,subQ14,subQ13,subQ12,subQ11,subQ10,subQ9,subQ8,subQ7,subQ6,subQ5,subQ4,subQ3,subQ2,subQ1,subQ0])]})]}),makeQuery(id+"F31.opExtrude","SWEPT_FACE",FACE,{"disambiguationData":[OSD([subQ27,subQ26,subQ25,subQ24,subQ23,subQ22,subQ21,subQ20,subQ19,subQ18,subQ17,subQ16,subQ15,subQ14,subQ13,subQ12,subQ11,subQ10,subQ9,subQ8,subQ7,subQ6,subQ5,subQ4,subQ3,subQ2,subQ1,subQ0])]})]});}
            var sketch = newSketch(context, id + "F35", { "sketchPlane" : qUnion([Q0])});
            skLineSegment(sketch, "E97.bottom", {"start": v(7, -28.5) * mm, "end": v(-7, -28.5) * mm});
            skLineSegment(sketch, "E97.top", {"start": v(7, -21.5) * mm, "end": v(-7, -21.5) * mm});
            skLineSegment(sketch, "E97.left", {"start": v(7, -28.5) * mm, "end": v(7, -21.5) * mm});
            skLineSegment(sketch, "E97.right", {"start": v(-7, -28.5) * mm, "end": v(-7, -21.5) * mm});
            skPoint(sketch, "E97.middle", {"position": v(0, -25) * mm});
            skLineSegment(sketch, "E98", {"start": v(0, 0) * mm, "end": v(0, -25) * mm});
            skSolve(sketch);
        }
        {
            var Q0;
            Q0=qSketchRegion(id+"F35",true);
            extrude(context, id + "F36", {"entities" : qUnion([Q0]), "operationType" : NewBodyOperationType.REMOVE, "oppositeDirection" : true, "depth" : 25 * mm, "offsetDistance" : 25 * mm});
        }
        {
            var Q0;
            {var subQ0=sQuery(id+"F15.wireOp",EDGE,"E41");Q0=makeQuery(id+"F28.boolean.opBoolean","MERGE",FACE,{"derivedFrom":[makeQuery(id+"F16.opExtrude","SWEPT_FACE",FACE,{"disambiguationData":[OSD([subQ0])]})],"fromTools":[makeQuery(id+"F28.opExtrude","SWEPT_FACE",FACE,{"disambiguationData":[OSD([subQ0])]})]});}
            extrude(context, id + "F37", {"entities" : qUnion([Q0]), "operationType" : NewBodyOperationType.ADD, "depth" : 2 * mm, "offsetDistance" : 25 * mm});
        }
        {
            var Q0;
            {var subQ0=sQuery(id+"F15.wireOp",EDGE,"E47.top");Q0=makeQuery(id+"F28.boolean.opBoolean","MERGE",FACE,{"derivedFrom":[makeQuery(id+"F16.opExtrude","SWEPT_FACE",FACE,{"disambiguationData":[OSD([subQ0])]})],"fromTools":[makeQuery(id+"F28.opExtrude","SWEPT_FACE",FACE,{"disambiguationData":[OSD([subQ0])]})]});}
            extrude(context, id + "F38", {"entities" : qUnion([Q0]), "operationType" : NewBodyOperationType.ADD, "depth" : 2 * mm, "offsetDistance" : 25 * mm});
        }
        {
            var Q0;
            {var subQ0=sQuery(id+"F15.wireOp",EDGE,"E55");Q0=makeQuery(id+"F28.boolean.opBoolean","MERGE",FACE,{"derivedFrom":[makeQuery(id+"F16.opExtrude","SWEPT_FACE",FACE,{"disambiguationData":[OSD([subQ0])]})],"fromTools":[makeQuery(id+"F28.opExtrude","SWEPT_FACE",FACE,{"disambiguationData":[OSD([subQ0])]})]});}
            extrude(context, id + "F39", {"entities" : qUnion([Q0]), "operationType" : NewBodyOperationType.ADD, "depth" : 2 * mm, "offsetDistance" : 25 * mm});
        }
        {
            var Q0;
            Q0=makeQuery(id+"F37.opExtrude","CAP_FACE",FACE,{"disambiguationData":[OSD([sQuery(id+"F15.wireOp",EDGE,"E41")])],"isStart":false});
            var sketch = newSketch(context, id + "F40", { "sketchPlane" : qUnion([Q0])});
            skLineSegment(sketch, "E99.bottom", {"start": v(-18, 46.7) * mm, "end": v(-13, 46.7) * mm});
            skLineSegment(sketch, "E99.top", {"start": v(-18, 34) * mm, "end": v(-13, 34) * mm});
            skLineSegment(sketch, "E99.left", {"start": v(-18, 46.7) * mm, "end": v(-18, 34) * mm});
            skLineSegment(sketch, "E99.right", {"start": v(-13, 46.7) * mm, "end": v(-13, 34) * mm});
            skLineSegment(sketch, "E100.bottom", {"start": v(18, 46.7) * mm, "end": v(13, 46.7) * mm});
            skLineSegment(sketch, "E100.top", {"start": v(18, 34) * mm, "end": v(13, 34) * mm});
            skLineSegment(sketch, "E100.left", {"start": v(18, 46.7) * mm, "end": v(18, 34) * mm});
            skLineSegment(sketch, "E100.right", {"start": v(13, 46.7) * mm, "end": v(13, 34) * mm});
            skSolve(sketch);
        }
        {
            var Q0;
            Q0=makeQuery(id+"F40.imprint","IMPRINT",FACE,{"disambiguationData":[TD([[makeQuery(id+"F40.imprint","IMPRINT",EDGE,{"derivedFrom":sQuery(id+"F40.wireOp",EDGE,"E99.bottom")}),1.0]])]});
            var Q1;
            Q1=makeQuery(id+"F40.imprint","IMPRINT",FACE,{"disambiguationData":[TD([[makeQuery(id+"F40.imprint","IMPRINT",EDGE,{"derivedFrom":sQuery(id+"F40.wireOp",EDGE,"E100.bottom")}),1.0]])]});
            extrude(context, id + "F41", {"entities" : qUnion([Q0, Q1]), "operationType" : NewBodyOperationType.ADD, "endBound" : BoundingType.UP_TO_NEXT, "depth" : 25 * mm, "offsetDistance" : 25 * mm});
        }
        {
            var Q0;
            Q0=makeQuery(id+"F41.opExtrude","SWEPT_FACE",FACE,{"disambiguationData":[OSD([sQuery(id+"F40.wireOp",EDGE,"E99.top")])]});
            extrude(context, id + "F42", {"entities" : qUnion([Q0]), "operationType" : NewBodyOperationType.REMOVE, "oppositeDirection" : true, "depth" : 25 * mm, "offsetDistance" : 25 * mm});
        }
        {
            var Q0;
            {var subQ0=sQuery(id+"F15.wireOp",EDGE,"E55");Q0=makeQuery(id+"F39.boolean.opBoolean","SPLIT",FACE,{"disambiguationData":[TD([makeQuery(id+"F33.opExtrude","SWEPT_FACE",FACE,{"disambiguationData":[OSD([sQuery(id+"F32.wireOp",EDGE,"E90")])]})])],"derivedFrom":makeQuery(id+"F39.opExtrude","CAP_FACE",FACE,{"disambiguationData":[OSD([subQ0])],"isStart":false})});}
            var sketch = newSketch(context, id + "F43", { "sketchPlane" : qUnion([Q0])});
            skLineSegment(sketch, "E101", {"start": v(-18, 34) * mm, "end": v(-18, 46.7) * mm});
            skLineSegment(sketch, "E102", {"start": v(-18, 46.7) * mm, "end": v(-14.1, 46.7) * mm});
            skLineSegment(sketch, "E103", {"start": v(-14.1, 46.7) * mm, "end": v(-14.1, 34) * mm});
            skLineSegment(sketch, "E104", {"start": v(-14.1, 34) * mm, "end": v(-18, 34) * mm});
            skSolve(sketch);
        }
        {
            var Q0;
            Q0=qSketchRegion(id+"F43",true);
            extrude(context, id + "F44", {"entities" : qUnion([Q0]), "operationType" : NewBodyOperationType.ADD, "endBound" : BoundingType.UP_TO_NEXT, "depth" : 25 * mm, "offsetDistance" : 25 * mm});
        }
        {
            var Q0;
            {var subQ0=sQuery(id+"F15.wireOp",EDGE,"E55");var subQ2=sQuery(id+"F15.wireOp",EDGE,"E52");Q0=makeQuery(id+"F39.boolean.opBoolean","SPLIT",FACE,{"disambiguationData":[TD([makeQuery(id+"F16.opExtrude","SWEPT_FACE",FACE,{"disambiguationData":[OSD([subQ2])]})])],"derivedFrom":makeQuery(id+"F39.opExtrude","CAP_FACE",FACE,{"disambiguationData":[OSD([subQ0])],"isStart":false})});}
            var sketch = newSketch(context, id + "F45", { "sketchPlane" : qUnion([Q0])});
            skLineSegment(sketch, "E105.bottom", {"start": v(18, 46.7) * mm, "end": v(13, 46.7) * mm});
            skLineSegment(sketch, "E105.top", {"start": v(18, 34) * mm, "end": v(13, 34) * mm});
            skLineSegment(sketch, "E105.left", {"start": v(18, 46.7) * mm, "end": v(18, 34) * mm});
            skLineSegment(sketch, "E105.right", {"start": v(13, 46.7) * mm, "end": v(13, 34) * mm});
            skSolve(sketch);
        }
        {
            var Q0;
            Q0=qSketchRegion(id+"F45",true);
            extrude(context, id + "F46", {"entities" : qUnion([Q0]), "operationType" : NewBodyOperationType.ADD, "endBound" : BoundingType.UP_TO_NEXT, "depth" : 25 * mm, "offsetDistance" : 25 * mm});
        }
        {
            var Q0;
            Q0=makeQuery(id+"F46.opExtrude","SWEPT_FACE",FACE,{"disambiguationData":[OSD([sQuery(id+"F45.wireOp",EDGE,"E105.top")])]});
            extrude(context, id + "F47", {"entities" : qUnion([Q0]), "operationType" : NewBodyOperationType.REMOVE, "oppositeDirection" : true, "depth" : 25 * mm, "offsetDistance" : 25 * mm});
        }
        {
            var Q0;
            Q0=makeQuery(id+"F38.opExtrude","CAP_FACE",FACE,{"disambiguationData":[OSD([sQuery(id+"F15.wireOp",EDGE,"E47.top")])],"isStart":false});
            var sketch = newSketch(context, id + "F48", { "sketchPlane" : qUnion([Q0])});
            skLineSegment(sketch, "E106.bottom", {"start": v(-18, 46.7) * mm, "end": v(-13, 46.7) * mm});
            skLineSegment(sketch, "E106.top", {"start": v(-18, 34) * mm, "end": v(-13, 34) * mm});
            skLineSegment(sketch, "E106.left", {"start": v(-18, 46.7) * mm, "end": v(-18, 34) * mm});
            skLineSegment(sketch, "E106.right", {"start": v(-13, 46.7) * mm, "end": v(-13, 34) * mm});
            skLineSegment(sketch, "E107.bottom", {"start": v(18, 46.7) * mm, "end": v(13, 46.7) * mm});
            skLineSegment(sketch, "E107.top", {"start": v(18, 34) * mm, "end": v(13, 34) * mm});
            skLineSegment(sketch, "E107.left", {"start": v(18, 46.7) * mm, "end": v(18, 34) * mm});
            skLineSegment(sketch, "E107.right", {"start": v(13, 46.7) * mm, "end": v(13, 34) * mm});
            skSolve(sketch);
        }
        {
            var Q0;
            Q0=qSketchRegion(id+"F48",true);
            extrude(context, id + "F49", {"entities" : qUnion([Q0]), "operationType" : NewBodyOperationType.ADD, "endBound" : BoundingType.UP_TO_NEXT, "depth" : 25 * mm, "offsetDistance" : 25 * mm});
        }
        {
            var Q0;
            {var subQ0=sQuery(id+"F15.wireOp",EDGE,"E41");var subQ1=makeQuery(id+"F37.opExtrude","CAP_FACE",FACE,{"disambiguationData":[OSD([subQ0])],"isStart":false});var subQ4=sQuery(id+"F13.wireOp",EDGE,"E19.3");var subQ5=sQuery(id+"F13.wireOp",EDGE,"E19.2");var subQ6=sQuery(id+"F13.wireOp",EDGE,"E19.5");var subQ7=sQuery(id+"F13.wireOp",EDGE,"E19.0");var subQ8=sQuery(id+"F15.wireOp",EDGE,"E52");var subQ9=sQuery(id+"F15.wireOp",EDGE,"E47.right");var subQ10=sQuery(id+"F6.wireOp",EDGE,"E14");var subQ12=sQuery(id+"F6.wireOp",EDGE,"E17");var subQ13=sQuery(id+"F6.wireOp",EDGE,"E13");var subQ16=sQuery(id+"F13.wireOp",EDGE,"E19.4");var subQ17=sQuery(id+"F6.wireOp",EDGE,"E16");var subQ18=sQuery(id+"F6.wireOp",EDGE,"E12");var subQ21=sQuery(id+"F15.wireOp",EDGE,"E55");var subQ22=sQuery(id+"F6.wireOp",EDGE,"E15");var subQ25=sQuery(id+"F13.wireOp",EDGE,"E19.1");var subQ28=sQuery(id+"F15.wireOp",EDGE,"E47.left");var subQ29=sQuery(id+"F15.wireOp",EDGE,"E47.top");var subQ31=sQuery(id+"F15.wireOp",EDGE,"E37");var subQ32=sQuery(id+"F15.wireOp",EDGE,"E39");var subQ33=sQuery(id+"F15.wireOp",EDGE,"E54");var subQ34=sQuery(id+"F4.wireOp",EDGE,"E2.right");var subQ35=sQuery(id+"F4.wireOp",EDGE,"E2.left");var subQ36=sQuery(id+"F4.wireOp",EDGE,"E2.top");var subQ37=sQuery(id+"F2.wireOp",EDGE,"E1.right");var subQ38=sQuery(id+"F2.wireOp",EDGE,"E1.left");var subQ39=sQuery(id+"F2.wireOp",EDGE,"E1.top");var subQ40=sQuery(id+"F2.wireOp",EDGE,"E1.bottom");Q0=makeQuery(id+"F41.boolean.opBoolean","SPLIT",FACE,{"disambiguationData":[TD([subQ1])],"derivedFrom":makeQuery(id+"F39.boolean.opBoolean","SPLIT",FACE,{"disambiguationData":[TD([makeQuery(id+"F14.opExtrude","SWEPT_FACE",FACE,{"disambiguationData":[OSD([subQ7])]})])],"derivedFrom":makeQuery(id+"F31.boolean.opBoolean","MERGE",FACE,{"derivedFrom":[makeQuery(id+"F30.boolean.opBoolean","MERGE",FACE,{"derivedFrom":[makeQuery(id+"F29.boolean.opBoolean","MERGE",FACE,{"derivedFrom":[makeQuery(id+"F28.boolean.opBoolean","COPY",FACE,{"derivedFrom":makeQuery(id+"F28.opExtrude","CAP_FACE",FACE,{"disambiguationData":[OSD([subQ40,subQ39,subQ38,subQ37,subQ36,subQ35,subQ34,subQ18,subQ13,subQ10,subQ22,subQ17,subQ12,subQ7,subQ25,subQ5,subQ4,subQ16,subQ6,subQ31,subQ32,subQ0,subQ29,subQ28,subQ9,subQ8,subQ33,subQ21])],"isStart":false})}),makeQuery(id+"F29.opExtrude","SWEPT_FACE",FACE,{"disambiguationData":[OSD([subQ40,subQ39,subQ38,subQ37,subQ36,subQ35,subQ34,subQ18,subQ13,subQ10,subQ22,subQ17,subQ12,subQ7,subQ25,subQ5,subQ4,subQ16,subQ6,subQ31,subQ32,subQ0,subQ29,subQ28,subQ9,subQ8,subQ33,subQ21])]})]}),makeQuery(id+"F30.opExtrude","SWEPT_FACE",FACE,{"disambiguationData":[OSD([subQ40,subQ39,subQ38,subQ37,subQ36,subQ35,subQ34,subQ18,subQ13,subQ10,subQ22,subQ17,subQ12,subQ7,subQ25,subQ5,subQ4,subQ16,subQ6,subQ31,subQ32,subQ0,subQ29,subQ28,subQ9,subQ8,subQ33,subQ21])]})]}),makeQuery(id+"F31.opExtrude","SWEPT_FACE",FACE,{"disambiguationData":[OSD([subQ40,subQ39,subQ38,subQ37,subQ36,subQ35,subQ34,subQ18,subQ13,subQ10,subQ22,subQ17,subQ12,subQ7,subQ25,subQ5,subQ4,subQ16,subQ6,subQ31,subQ32,subQ0,subQ29,subQ28,subQ9,subQ8,subQ33,subQ21])]})]})})});}
            var Q1;
            {var subQ0=sQuery(id+"F13.wireOp",EDGE,"E19.5");var subQ1=sQuery(id+"F13.wireOp",EDGE,"E19.0");var subQ3=sQuery(id+"F15.wireOp",EDGE,"E41");var subQ4=sQuery(id+"F15.wireOp",EDGE,"E39");var subQ9=sQuery(id+"F6.wireOp",EDGE,"E14");var subQ11=sQuery(id+"F6.wireOp",EDGE,"E17");var subQ12=sQuery(id+"F6.wireOp",EDGE,"E13");var subQ15=sQuery(id+"F13.wireOp",EDGE,"E19.4");var subQ19=sQuery(id+"F15.wireOp",EDGE,"E52");var subQ23=makeQuery(id+"F14.opExtrude","SWEPT_FACE",FACE,{"disambiguationData":[OSD([subQ1])]});var subQ25=sQuery(id+"F15.wireOp",EDGE,"E55");var subQ27=sQuery(id+"F13.wireOp",EDGE,"E19.1");var subQ28=sQuery(id+"F6.wireOp",EDGE,"E15");var subQ33=sQuery(id+"F13.wireOp",EDGE,"E19.2");var subQ42=sQuery(id+"F13.wireOp",EDGE,"E19.3");var subQ43=sQuery(id+"F15.wireOp",EDGE,"E47.right");var subQ44=sQuery(id+"F6.wireOp",EDGE,"E16");var subQ45=sQuery(id+"F6.wireOp",EDGE,"E12");var subQ49=sQuery(id+"F15.wireOp",EDGE,"E47.left");var subQ50=sQuery(id+"F15.wireOp",EDGE,"E47.top");var subQ51=sQuery(id+"F15.wireOp",EDGE,"E37");var subQ52=sQuery(id+"F15.wireOp",EDGE,"E54");var subQ53=sQuery(id+"F4.wireOp",EDGE,"E2.right");var subQ54=sQuery(id+"F4.wireOp",EDGE,"E2.left");var subQ55=sQuery(id+"F4.wireOp",EDGE,"E2.top");var subQ56=sQuery(id+"F2.wireOp",EDGE,"E1.right");var subQ57=sQuery(id+"F2.wireOp",EDGE,"E1.left");var subQ58=sQuery(id+"F2.wireOp",EDGE,"E1.top");var subQ59=sQuery(id+"F2.wireOp",EDGE,"E1.bottom");Q1=makeQuery(id+"F46.boolean.opBoolean","SPLIT",FACE,{"disambiguationData":[TD([subQ23])],"derivedFrom":makeQuery(id+"F41.boolean.opBoolean","SPLIT",FACE,{"disambiguationData":[TD([subQ23])],"derivedFrom":makeQuery(id+"F39.boolean.opBoolean","SPLIT",FACE,{"disambiguationData":[TD([subQ23])],"derivedFrom":makeQuery(id+"F31.boolean.opBoolean","MERGE",FACE,{"derivedFrom":[makeQuery(id+"F30.boolean.opBoolean","MERGE",FACE,{"derivedFrom":[makeQuery(id+"F29.boolean.opBoolean","MERGE",FACE,{"derivedFrom":[makeQuery(id+"F28.boolean.opBoolean","COPY",FACE,{"derivedFrom":makeQuery(id+"F28.opExtrude","CAP_FACE",FACE,{"disambiguationData":[OSD([subQ59,subQ58,subQ57,subQ56,subQ55,subQ54,subQ53,subQ45,subQ12,subQ9,subQ28,subQ44,subQ11,subQ1,subQ27,subQ33,subQ42,subQ15,subQ0,subQ51,subQ4,subQ3,subQ50,subQ49,subQ43,subQ19,subQ52,subQ25])],"isStart":false})}),makeQuery(id+"F29.opExtrude","SWEPT_FACE",FACE,{"disambiguationData":[OSD([subQ59,subQ58,subQ57,subQ56,subQ55,subQ54,subQ53,subQ45,subQ12,subQ9,subQ28,subQ44,subQ11,subQ1,subQ27,subQ33,subQ42,subQ15,subQ0,subQ51,subQ4,subQ3,subQ50,subQ49,subQ43,subQ19,subQ52,subQ25])]})]}),makeQuery(id+"F30.opExtrude","SWEPT_FACE",FACE,{"disambiguationData":[OSD([subQ59,subQ58,subQ57,subQ56,subQ55,subQ54,subQ53,subQ45,subQ12,subQ9,subQ28,subQ44,subQ11,subQ1,subQ27,subQ33,subQ42,subQ15,subQ0,subQ51,subQ4,subQ3,subQ50,subQ49,subQ43,subQ19,subQ52,subQ25])]})]}),makeQuery(id+"F31.opExtrude","SWEPT_FACE",FACE,{"disambiguationData":[OSD([subQ59,subQ58,subQ57,subQ56,subQ55,subQ54,subQ53,subQ45,subQ12,subQ9,subQ28,subQ44,subQ11,subQ1,subQ27,subQ33,subQ42,subQ15,subQ0,subQ51,subQ4,subQ3,subQ50,subQ49,subQ43,subQ19,subQ52,subQ25])]})]})})})});}
            var Q2;
            {var subQ1=sQuery(id+"F15.wireOp",EDGE,"E39");var subQ4=makeQuery(id+"F33.opExtrude","SWEPT_FACE",FACE,{"disambiguationData":[OSD([sQuery(id+"F32.wireOp",EDGE,"E87")])]});var subQ5=sQuery(id+"F15.wireOp",EDGE,"E41");var subQ7=sQuery(id+"F15.wireOp",EDGE,"E55");var subQ11=sQuery(id+"F13.wireOp",EDGE,"E19.1");var subQ12=sQuery(id+"F13.wireOp",EDGE,"E19.0");var subQ16=sQuery(id+"F6.wireOp",EDGE,"E15");var subQ18=sQuery(id+"F6.wireOp",EDGE,"E14");var subQ21=sQuery(id+"F13.wireOp",EDGE,"E19.2");var subQ26=sQuery(id+"F15.wireOp",EDGE,"E52");var subQ28=makeQuery(id+"F14.opExtrude","SWEPT_FACE",FACE,{"disambiguationData":[OSD([subQ12])]});var subQ29=sQuery(id+"F13.wireOp",EDGE,"E19.5");var subQ30=sQuery(id+"F6.wireOp",EDGE,"E17");var subQ31=sQuery(id+"F6.wireOp",EDGE,"E13");var subQ37=sQuery(id+"F13.wireOp",EDGE,"E19.4");var subQ42=sQuery(id+"F13.wireOp",EDGE,"E19.3");var subQ43=sQuery(id+"F15.wireOp",EDGE,"E47.right");var subQ44=sQuery(id+"F6.wireOp",EDGE,"E16");var subQ45=sQuery(id+"F6.wireOp",EDGE,"E12");var subQ49=sQuery(id+"F15.wireOp",EDGE,"E47.left");var subQ50=sQuery(id+"F15.wireOp",EDGE,"E47.top");var subQ51=sQuery(id+"F15.wireOp",EDGE,"E37");var subQ52=sQuery(id+"F15.wireOp",EDGE,"E54");var subQ53=sQuery(id+"F4.wireOp",EDGE,"E2.right");var subQ54=sQuery(id+"F4.wireOp",EDGE,"E2.left");var subQ55=sQuery(id+"F4.wireOp",EDGE,"E2.top");var subQ56=sQuery(id+"F2.wireOp",EDGE,"E1.right");var subQ57=sQuery(id+"F2.wireOp",EDGE,"E1.left");var subQ58=sQuery(id+"F2.wireOp",EDGE,"E1.top");var subQ59=sQuery(id+"F2.wireOp",EDGE,"E1.bottom");Q2=makeQuery(id+"F46.boolean.opBoolean","SPLIT",FACE,{"disambiguationData":[TD([subQ4])],"derivedFrom":makeQuery(id+"F41.boolean.opBoolean","SPLIT",FACE,{"disambiguationData":[TD([subQ28])],"derivedFrom":makeQuery(id+"F39.boolean.opBoolean","SPLIT",FACE,{"disambiguationData":[TD([subQ28])],"derivedFrom":makeQuery(id+"F31.boolean.opBoolean","MERGE",FACE,{"derivedFrom":[makeQuery(id+"F30.boolean.opBoolean","MERGE",FACE,{"derivedFrom":[makeQuery(id+"F29.boolean.opBoolean","MERGE",FACE,{"derivedFrom":[makeQuery(id+"F28.boolean.opBoolean","COPY",FACE,{"derivedFrom":makeQuery(id+"F28.opExtrude","CAP_FACE",FACE,{"disambiguationData":[OSD([subQ59,subQ58,subQ57,subQ56,subQ55,subQ54,subQ53,subQ45,subQ31,subQ18,subQ16,subQ44,subQ30,subQ12,subQ11,subQ21,subQ42,subQ37,subQ29,subQ51,subQ1,subQ5,subQ50,subQ49,subQ43,subQ26,subQ52,subQ7])],"isStart":false})}),makeQuery(id+"F29.opExtrude","SWEPT_FACE",FACE,{"disambiguationData":[OSD([subQ59,subQ58,subQ57,subQ56,subQ55,subQ54,subQ53,subQ45,subQ31,subQ18,subQ16,subQ44,subQ30,subQ12,subQ11,subQ21,subQ42,subQ37,subQ29,subQ51,subQ1,subQ5,subQ50,subQ49,subQ43,subQ26,subQ52,subQ7])]})]}),makeQuery(id+"F30.opExtrude","SWEPT_FACE",FACE,{"disambiguationData":[OSD([subQ59,subQ58,subQ57,subQ56,subQ55,subQ54,subQ53,subQ45,subQ31,subQ18,subQ16,subQ44,subQ30,subQ12,subQ11,subQ21,subQ42,subQ37,subQ29,subQ51,subQ1,subQ5,subQ50,subQ49,subQ43,subQ26,subQ52,subQ7])]})]}),makeQuery(id+"F31.opExtrude","SWEPT_FACE",FACE,{"disambiguationData":[OSD([subQ59,subQ58,subQ57,subQ56,subQ55,subQ54,subQ53,subQ45,subQ31,subQ18,subQ16,subQ44,subQ30,subQ12,subQ11,subQ21,subQ42,subQ37,subQ29,subQ51,subQ1,subQ5,subQ50,subQ49,subQ43,subQ26,subQ52,subQ7])]})]})})})});}
            var Q3;
            {var subQ0=sQuery(id+"F15.wireOp",EDGE,"E55");var subQ1=sQuery(id+"F15.wireOp",EDGE,"E54");var subQ2=sQuery(id+"F13.wireOp",EDGE,"E19.4");var subQ3=sQuery(id+"F6.wireOp",EDGE,"E17");var subQ4=sQuery(id+"F6.wireOp",EDGE,"E13");var subQ6=sQuery(id+"F6.wireOp",EDGE,"E16");var subQ7=sQuery(id+"F6.wireOp",EDGE,"E12");var subQ9=sQuery(id+"F13.wireOp",EDGE,"E19.5");var subQ11=sQuery(id+"F13.wireOp",EDGE,"E19.3");var subQ12=sQuery(id+"F6.wireOp",EDGE,"E14");var subQ14=sQuery(id+"F13.wireOp",EDGE,"E19.0");var subQ15=sQuery(id+"F15.wireOp",EDGE,"E52");var subQ16=sQuery(id+"F15.wireOp",EDGE,"E47.right");var subQ17=sQuery(id+"F15.wireOp",EDGE,"E47.left");var subQ18=sQuery(id+"F15.wireOp",EDGE,"E47.top");var subQ19=sQuery(id+"F15.wireOp",EDGE,"E41");var subQ20=sQuery(id+"F15.wireOp",EDGE,"E39");var subQ21=sQuery(id+"F15.wireOp",EDGE,"E37");var subQ22=sQuery(id+"F13.wireOp",EDGE,"E19.2");var subQ23=sQuery(id+"F13.wireOp",EDGE,"E19.1");var subQ24=sQuery(id+"F6.wireOp",EDGE,"E15");var subQ25=sQuery(id+"F4.wireOp",EDGE,"E2.right");var subQ26=sQuery(id+"F4.wireOp",EDGE,"E2.left");var subQ27=sQuery(id+"F4.wireOp",EDGE,"E2.top");var subQ28=sQuery(id+"F2.wireOp",EDGE,"E1.right");var subQ29=sQuery(id+"F2.wireOp",EDGE,"E1.left");var subQ30=sQuery(id+"F2.wireOp",EDGE,"E1.top");var subQ31=sQuery(id+"F2.wireOp",EDGE,"E1.bottom");Q3=makeQuery(id+"F39.boolean.opBoolean","SPLIT",FACE,{"disambiguationData":[TD([makeQuery(id+"F16.opExtrude","SWEPT_FACE",FACE,{"disambiguationData":[OSD([subQ1])]})])],"derivedFrom":makeQuery(id+"F31.boolean.opBoolean","MERGE",FACE,{"derivedFrom":[makeQuery(id+"F30.boolean.opBoolean","MERGE",FACE,{"derivedFrom":[makeQuery(id+"F29.boolean.opBoolean","MERGE",FACE,{"derivedFrom":[makeQuery(id+"F28.boolean.opBoolean","COPY",FACE,{"derivedFrom":makeQuery(id+"F28.opExtrude","CAP_FACE",FACE,{"disambiguationData":[OSD([subQ31,subQ30,subQ29,subQ28,subQ27,subQ26,subQ25,subQ7,subQ4,subQ12,subQ24,subQ6,subQ3,subQ14,subQ23,subQ22,subQ11,subQ2,subQ9,subQ21,subQ20,subQ19,subQ18,subQ17,subQ16,subQ15,subQ1,subQ0])],"isStart":false})}),makeQuery(id+"F29.opExtrude","SWEPT_FACE",FACE,{"disambiguationData":[OSD([subQ31,subQ30,subQ29,subQ28,subQ27,subQ26,subQ25,subQ7,subQ4,subQ12,subQ24,subQ6,subQ3,subQ14,subQ23,subQ22,subQ11,subQ2,subQ9,subQ21,subQ20,subQ19,subQ18,subQ17,subQ16,subQ15,subQ1,subQ0])]})]}),makeQuery(id+"F30.opExtrude","SWEPT_FACE",FACE,{"disambiguationData":[OSD([subQ31,subQ30,subQ29,subQ28,subQ27,subQ26,subQ25,subQ7,subQ4,subQ12,subQ24,subQ6,subQ3,subQ14,subQ23,subQ22,subQ11,subQ2,subQ9,subQ21,subQ20,subQ19,subQ18,subQ17,subQ16,subQ15,subQ1,subQ0])]})]}),makeQuery(id+"F31.opExtrude","SWEPT_FACE",FACE,{"disambiguationData":[OSD([subQ31,subQ30,subQ29,subQ28,subQ27,subQ26,subQ25,subQ7,subQ4,subQ12,subQ24,subQ6,subQ3,subQ14,subQ23,subQ22,subQ11,subQ2,subQ9,subQ21,subQ20,subQ19,subQ18,subQ17,subQ16,subQ15,subQ1,subQ0])]})]})});}
            var Q4;
            {var subQ1=sQuery(id+"F13.wireOp",EDGE,"E19.3");var subQ2=makeQuery(id+"F14.opExtrude","SWEPT_FACE",FACE,{"disambiguationData":[OSD([subQ1])]});var subQ3=sQuery(id+"F15.wireOp",EDGE,"E47.right");var subQ4=sQuery(id+"F15.wireOp",EDGE,"E47.top");var subQ6=sQuery(id+"F13.wireOp",EDGE,"E19.4");var subQ7=sQuery(id+"F6.wireOp",EDGE,"E17");var subQ8=sQuery(id+"F6.wireOp",EDGE,"E13");var subQ10=sQuery(id+"F6.wireOp",EDGE,"E16");var subQ11=sQuery(id+"F6.wireOp",EDGE,"E12");var subQ14=sQuery(id+"F13.wireOp",EDGE,"E19.5");var subQ18=makeQuery(id+"F16.opExtrude","SWEPT_FACE",FACE,{"disambiguationData":[OSD([subQ3])]});var subQ22=sQuery(id+"F15.wireOp",EDGE,"E47.left");var subQ24=sQuery(id+"F13.wireOp",EDGE,"E19.1");var subQ25=sQuery(id+"F6.wireOp",EDGE,"E15");var subQ27=sQuery(id+"F6.wireOp",EDGE,"E14");var subQ30=sQuery(id+"F13.wireOp",EDGE,"E19.2");var subQ33=sQuery(id+"F15.wireOp",EDGE,"E41");var subQ34=sQuery(id+"F15.wireOp",EDGE,"E37");var subQ43=sQuery(id+"F13.wireOp",EDGE,"E19.0");var subQ48=sQuery(id+"F15.wireOp",EDGE,"E52");var subQ50=sQuery(id+"F15.wireOp",EDGE,"E55");var subQ51=sQuery(id+"F15.wireOp",EDGE,"E39");var subQ52=sQuery(id+"F15.wireOp",EDGE,"E54");var subQ53=sQuery(id+"F4.wireOp",EDGE,"E2.right");var subQ54=sQuery(id+"F4.wireOp",EDGE,"E2.left");var subQ55=sQuery(id+"F4.wireOp",EDGE,"E2.top");var subQ56=sQuery(id+"F2.wireOp",EDGE,"E1.right");var subQ57=sQuery(id+"F2.wireOp",EDGE,"E1.left");var subQ58=sQuery(id+"F2.wireOp",EDGE,"E1.top");var subQ59=sQuery(id+"F2.wireOp",EDGE,"E1.bottom");Q4=makeQuery(id+"F49.boolean.opBoolean","SPLIT",FACE,{"disambiguationData":[TD([subQ18])],"derivedFrom":makeQuery(id+"F41.boolean.opBoolean","SPLIT",FACE,{"disambiguationData":[TD([subQ2])],"derivedFrom":makeQuery(id+"F39.boolean.opBoolean","SPLIT",FACE,{"disambiguationData":[TD([makeQuery(id+"F14.opExtrude","SWEPT_FACE",FACE,{"disambiguationData":[OSD([subQ43])]})])],"derivedFrom":makeQuery(id+"F31.boolean.opBoolean","MERGE",FACE,{"derivedFrom":[makeQuery(id+"F30.boolean.opBoolean","MERGE",FACE,{"derivedFrom":[makeQuery(id+"F29.boolean.opBoolean","MERGE",FACE,{"derivedFrom":[makeQuery(id+"F28.boolean.opBoolean","COPY",FACE,{"derivedFrom":makeQuery(id+"F28.opExtrude","CAP_FACE",FACE,{"disambiguationData":[OSD([subQ59,subQ58,subQ57,subQ56,subQ55,subQ54,subQ53,subQ11,subQ8,subQ27,subQ25,subQ10,subQ7,subQ43,subQ24,subQ30,subQ1,subQ6,subQ14,subQ34,subQ51,subQ33,subQ4,subQ22,subQ3,subQ48,subQ52,subQ50])],"isStart":false})}),makeQuery(id+"F29.opExtrude","SWEPT_FACE",FACE,{"disambiguationData":[OSD([subQ59,subQ58,subQ57,subQ56,subQ55,subQ54,subQ53,subQ11,subQ8,subQ27,subQ25,subQ10,subQ7,subQ43,subQ24,subQ30,subQ1,subQ6,subQ14,subQ34,subQ51,subQ33,subQ4,subQ22,subQ3,subQ48,subQ52,subQ50])]})]}),makeQuery(id+"F30.opExtrude","SWEPT_FACE",FACE,{"disambiguationData":[OSD([subQ59,subQ58,subQ57,subQ56,subQ55,subQ54,subQ53,subQ11,subQ8,subQ27,subQ25,subQ10,subQ7,subQ43,subQ24,subQ30,subQ1,subQ6,subQ14,subQ34,subQ51,subQ33,subQ4,subQ22,subQ3,subQ48,subQ52,subQ50])]})]}),makeQuery(id+"F31.opExtrude","SWEPT_FACE",FACE,{"disambiguationData":[OSD([subQ59,subQ58,subQ57,subQ56,subQ55,subQ54,subQ53,subQ11,subQ8,subQ27,subQ25,subQ10,subQ7,subQ43,subQ24,subQ30,subQ1,subQ6,subQ14,subQ34,subQ51,subQ33,subQ4,subQ22,subQ3,subQ48,subQ52,subQ50])]})]})})})});}
            var Q5;
            {var subQ1=sQuery(id+"F15.wireOp",EDGE,"E37");var subQ2=makeQuery(id+"F16.opExtrude","SWEPT_FACE",FACE,{"disambiguationData":[OSD([subQ1])]});var subQ3=sQuery(id+"F13.wireOp",EDGE,"E19.2");var subQ4=sQuery(id+"F13.wireOp",EDGE,"E19.1");var subQ7=sQuery(id+"F13.wireOp",EDGE,"E19.3");var subQ8=makeQuery(id+"F14.opExtrude","SWEPT_FACE",FACE,{"disambiguationData":[OSD([subQ7])]});var subQ9=sQuery(id+"F6.wireOp",EDGE,"E15");var subQ11=sQuery(id+"F6.wireOp",EDGE,"E14");var subQ14=sQuery(id+"F13.wireOp",EDGE,"E19.0");var subQ16=sQuery(id+"F6.wireOp",EDGE,"E16");var subQ17=sQuery(id+"F6.wireOp",EDGE,"E12");var subQ21=sQuery(id+"F15.wireOp",EDGE,"E47.left");var subQ27=sQuery(id+"F15.wireOp",EDGE,"E41");var subQ29=sQuery(id+"F15.wireOp",EDGE,"E47.top");var subQ32=sQuery(id+"F15.wireOp",EDGE,"E47.right");var subQ36=sQuery(id+"F13.wireOp",EDGE,"E19.4");var subQ41=sQuery(id+"F6.wireOp",EDGE,"E17");var subQ42=sQuery(id+"F6.wireOp",EDGE,"E13");var subQ46=sQuery(id+"F13.wireOp",EDGE,"E19.5");var subQ49=sQuery(id+"F15.wireOp",EDGE,"E52");var subQ51=sQuery(id+"F15.wireOp",EDGE,"E55");var subQ52=sQuery(id+"F15.wireOp",EDGE,"E39");var subQ53=sQuery(id+"F15.wireOp",EDGE,"E54");var subQ54=sQuery(id+"F4.wireOp",EDGE,"E2.right");var subQ55=sQuery(id+"F4.wireOp",EDGE,"E2.left");var subQ56=sQuery(id+"F4.wireOp",EDGE,"E2.top");var subQ57=sQuery(id+"F2.wireOp",EDGE,"E1.right");var subQ58=sQuery(id+"F2.wireOp",EDGE,"E1.left");var subQ59=sQuery(id+"F2.wireOp",EDGE,"E1.top");var subQ60=sQuery(id+"F2.wireOp",EDGE,"E1.bottom");Q5=makeQuery(id+"F49.boolean.opBoolean","SPLIT",FACE,{"disambiguationData":[TD([subQ2])],"derivedFrom":makeQuery(id+"F41.boolean.opBoolean","SPLIT",FACE,{"disambiguationData":[TD([subQ8])],"derivedFrom":makeQuery(id+"F39.boolean.opBoolean","SPLIT",FACE,{"disambiguationData":[TD([makeQuery(id+"F14.opExtrude","SWEPT_FACE",FACE,{"disambiguationData":[OSD([subQ14])]})])],"derivedFrom":makeQuery(id+"F31.boolean.opBoolean","MERGE",FACE,{"derivedFrom":[makeQuery(id+"F30.boolean.opBoolean","MERGE",FACE,{"derivedFrom":[makeQuery(id+"F29.boolean.opBoolean","MERGE",FACE,{"derivedFrom":[makeQuery(id+"F28.boolean.opBoolean","COPY",FACE,{"derivedFrom":makeQuery(id+"F28.opExtrude","CAP_FACE",FACE,{"disambiguationData":[OSD([subQ60,subQ59,subQ58,subQ57,subQ56,subQ55,subQ54,subQ17,subQ42,subQ11,subQ9,subQ16,subQ41,subQ14,subQ4,subQ3,subQ7,subQ36,subQ46,subQ1,subQ52,subQ27,subQ29,subQ21,subQ32,subQ49,subQ53,subQ51])],"isStart":false})}),makeQuery(id+"F29.opExtrude","SWEPT_FACE",FACE,{"disambiguationData":[OSD([subQ60,subQ59,subQ58,subQ57,subQ56,subQ55,subQ54,subQ17,subQ42,subQ11,subQ9,subQ16,subQ41,subQ14,subQ4,subQ3,subQ7,subQ36,subQ46,subQ1,subQ52,subQ27,subQ29,subQ21,subQ32,subQ49,subQ53,subQ51])]})]}),makeQuery(id+"F30.opExtrude","SWEPT_FACE",FACE,{"disambiguationData":[OSD([subQ60,subQ59,subQ58,subQ57,subQ56,subQ55,subQ54,subQ17,subQ42,subQ11,subQ9,subQ16,subQ41,subQ14,subQ4,subQ3,subQ7,subQ36,subQ46,subQ1,subQ52,subQ27,subQ29,subQ21,subQ32,subQ49,subQ53,subQ51])]})]}),makeQuery(id+"F31.opExtrude","SWEPT_FACE",FACE,{"disambiguationData":[OSD([subQ60,subQ59,subQ58,subQ57,subQ56,subQ55,subQ54,subQ17,subQ42,subQ11,subQ9,subQ16,subQ41,subQ14,subQ4,subQ3,subQ7,subQ36,subQ46,subQ1,subQ52,subQ27,subQ29,subQ21,subQ32,subQ49,subQ53,subQ51])]})]})})})});}
            var Q6;
            {var subQ1=sQuery(id+"F15.wireOp",EDGE,"E47.top");var subQ2=makeQuery(id+"F38.opExtrude","CAP_FACE",FACE,{"disambiguationData":[OSD([subQ1])],"isStart":false});var subQ3=sQuery(id+"F15.wireOp",EDGE,"E47.right");var subQ5=sQuery(id+"F15.wireOp",EDGE,"E47.left");var subQ7=sQuery(id+"F13.wireOp",EDGE,"E19.1");var subQ8=sQuery(id+"F6.wireOp",EDGE,"E15");var subQ10=sQuery(id+"F6.wireOp",EDGE,"E14");var subQ13=sQuery(id+"F13.wireOp",EDGE,"E19.2");var subQ16=sQuery(id+"F15.wireOp",EDGE,"E41");var subQ17=sQuery(id+"F15.wireOp",EDGE,"E37");var subQ19=sQuery(id+"F6.wireOp",EDGE,"E16");var subQ20=sQuery(id+"F6.wireOp",EDGE,"E12");var subQ23=sQuery(id+"F13.wireOp",EDGE,"E19.3");var subQ25=sQuery(id+"F13.wireOp",EDGE,"E19.4");var subQ33=sQuery(id+"F13.wireOp",EDGE,"E19.0");var subQ35=makeQuery(id+"F14.opExtrude","SWEPT_FACE",FACE,{"disambiguationData":[OSD([subQ23])]});var subQ38=sQuery(id+"F6.wireOp",EDGE,"E17");var subQ39=sQuery(id+"F6.wireOp",EDGE,"E13");var subQ44=sQuery(id+"F13.wireOp",EDGE,"E19.5");var subQ48=sQuery(id+"F15.wireOp",EDGE,"E52");var subQ50=sQuery(id+"F15.wireOp",EDGE,"E55");var subQ51=sQuery(id+"F15.wireOp",EDGE,"E39");var subQ52=sQuery(id+"F15.wireOp",EDGE,"E54");var subQ53=sQuery(id+"F4.wireOp",EDGE,"E2.right");var subQ54=sQuery(id+"F4.wireOp",EDGE,"E2.left");var subQ55=sQuery(id+"F4.wireOp",EDGE,"E2.top");var subQ56=sQuery(id+"F2.wireOp",EDGE,"E1.right");var subQ57=sQuery(id+"F2.wireOp",EDGE,"E1.left");var subQ58=sQuery(id+"F2.wireOp",EDGE,"E1.top");var subQ59=sQuery(id+"F2.wireOp",EDGE,"E1.bottom");Q6=makeQuery(id+"F49.boolean.opBoolean","SPLIT",FACE,{"disambiguationData":[TD([subQ2])],"derivedFrom":makeQuery(id+"F41.boolean.opBoolean","SPLIT",FACE,{"disambiguationData":[TD([subQ35])],"derivedFrom":makeQuery(id+"F39.boolean.opBoolean","SPLIT",FACE,{"disambiguationData":[TD([makeQuery(id+"F14.opExtrude","SWEPT_FACE",FACE,{"disambiguationData":[OSD([subQ33])]})])],"derivedFrom":makeQuery(id+"F31.boolean.opBoolean","MERGE",FACE,{"derivedFrom":[makeQuery(id+"F30.boolean.opBoolean","MERGE",FACE,{"derivedFrom":[makeQuery(id+"F29.boolean.opBoolean","MERGE",FACE,{"derivedFrom":[makeQuery(id+"F28.boolean.opBoolean","COPY",FACE,{"derivedFrom":makeQuery(id+"F28.opExtrude","CAP_FACE",FACE,{"disambiguationData":[OSD([subQ59,subQ58,subQ57,subQ56,subQ55,subQ54,subQ53,subQ20,subQ39,subQ10,subQ8,subQ19,subQ38,subQ33,subQ7,subQ13,subQ23,subQ25,subQ44,subQ17,subQ51,subQ16,subQ1,subQ5,subQ3,subQ48,subQ52,subQ50])],"isStart":false})}),makeQuery(id+"F29.opExtrude","SWEPT_FACE",FACE,{"disambiguationData":[OSD([subQ59,subQ58,subQ57,subQ56,subQ55,subQ54,subQ53,subQ20,subQ39,subQ10,subQ8,subQ19,subQ38,subQ33,subQ7,subQ13,subQ23,subQ25,subQ44,subQ17,subQ51,subQ16,subQ1,subQ5,subQ3,subQ48,subQ52,subQ50])]})]}),makeQuery(id+"F30.opExtrude","SWEPT_FACE",FACE,{"disambiguationData":[OSD([subQ59,subQ58,subQ57,subQ56,subQ55,subQ54,subQ53,subQ20,subQ39,subQ10,subQ8,subQ19,subQ38,subQ33,subQ7,subQ13,subQ23,subQ25,subQ44,subQ17,subQ51,subQ16,subQ1,subQ5,subQ3,subQ48,subQ52,subQ50])]})]}),makeQuery(id+"F31.opExtrude","SWEPT_FACE",FACE,{"disambiguationData":[OSD([subQ59,subQ58,subQ57,subQ56,subQ55,subQ54,subQ53,subQ20,subQ39,subQ10,subQ8,subQ19,subQ38,subQ33,subQ7,subQ13,subQ23,subQ25,subQ44,subQ17,subQ51,subQ16,subQ1,subQ5,subQ3,subQ48,subQ52,subQ50])]})]})})})});}
            extrude(context, id + "F50", {"entities" : qUnion([Q0, Q1, Q2, Q3, Q4, Q5, Q6]), "operationType" : NewBodyOperationType.REMOVE, "oppositeDirection" : true, "depth" : 25 * mm, "offsetDistance" : 25 * mm});
        }
        {
            var Q0;
            {var subQ0=sQuery(id+"F35.wireOp",EDGE,"E97.right");Q0=makeQuery(id+"F42.boolean.opBoolean","MERGE",FACE,{"derivedFrom":[makeQuery(id+"F36.boolean.opBoolean","COPY",FACE,{"derivedFrom":makeQuery(id+"F36.opExtrude","SWEPT_FACE",FACE,{"disambiguationData":[OSD([subQ0])]})})],"fromTools":[makeQuery(id+"F42.opExtrude","SWEPT_FACE",FACE,{"disambiguationData":[OSD([subQ0])]})]});}
            extrude(context, id + "F51", {"entities" : qUnion([Q0]), "operationType" : NewBodyOperationType.ADD, "endBound" : BoundingType.UP_TO_NEXT, "depth" : 25 * mm, "offsetDistance" : 25 * mm});
        }
        {
            var Q0;
            {var subQ2=sQuery(id+"F15.wireOp",EDGE,"E55");var subQ4=sQuery(id+"F15.wireOp",EDGE,"E52");var subQ8=sQuery(id+"F15.wireOp",EDGE,"E39");Q0=makeQuery(id+"F47.boolean.opBoolean","SPLIT",FACE,{"disambiguationData":[TD([makeQuery(id+"F16.opExtrude","SWEPT_FACE",FACE,{"disambiguationData":[OSD([subQ8])]})])],"derivedFrom":makeQuery(id+"F46.boolean.opBoolean","MERGE",FACE,{"derivedFrom":[makeQuery(id+"F39.boolean.opBoolean","MERGE",FACE,{"derivedFrom":[makeQuery(id+"F28.boolean.opBoolean","MERGE",FACE,{"derivedFrom":[makeQuery(id+"F16.opExtrude","SWEPT_FACE",FACE,{"disambiguationData":[OSD([subQ4])]})],"fromTools":[makeQuery(id+"F28.opExtrude","SWEPT_FACE",FACE,{"disambiguationData":[OSD([subQ4])]})]}),makeQuery(id+"F39.opExtrude","SWEPT_FACE",FACE,{"disambiguationData":[OSD([subQ4,subQ2])]})]}),makeQuery(id+"F46.opExtrude","SWEPT_FACE",FACE,{"disambiguationData":[OSD([sQuery(id+"F45.wireOp",EDGE,"E105.left")])]})]})});}
            extrude(context, id + "F52", {"entities" : qUnion([Q0]), "operationType" : NewBodyOperationType.ADD, "endBound" : BoundingType.UP_TO_NEXT, "depth" : 25 * mm, "offsetDistance" : 25 * mm});
        }
        {
            var Q0;
            {var subQ2=sQuery(id+"F15.wireOp",EDGE,"E52");var subQ3=sQuery(id+"F15.wireOp",EDGE,"E41");var subQ11=sQuery(id+"F15.wireOp",EDGE,"E39");Q0=makeQuery(id+"F46.boolean.opBoolean","SPLIT",FACE,{"disambiguationData":[TD([makeQuery(id+"F16.opExtrude","SWEPT_FACE",FACE,{"disambiguationData":[OSD([subQ2])]})])],"derivedFrom":makeQuery(id+"F42.boolean.opBoolean","SPLIT",FACE,{"disambiguationData":[TD([makeQuery(id+"F33.opExtrude","SWEPT_FACE",FACE,{"disambiguationData":[OSD([sQuery(id+"F32.wireOp",EDGE,"E87")])]})])],"derivedFrom":makeQuery(id+"F41.boolean.opBoolean","MERGE",FACE,{"derivedFrom":[makeQuery(id+"F37.boolean.opBoolean","MERGE",FACE,{"derivedFrom":[makeQuery(id+"F28.boolean.opBoolean","MERGE",FACE,{"derivedFrom":[makeQuery(id+"F16.opExtrude","SWEPT_FACE",FACE,{"disambiguationData":[OSD([subQ11])]})],"fromTools":[makeQuery(id+"F28.opExtrude","SWEPT_FACE",FACE,{"disambiguationData":[OSD([subQ11])]})]}),makeQuery(id+"F37.opExtrude","SWEPT_FACE",FACE,{"disambiguationData":[OSD([subQ11,subQ3])]})]}),makeQuery(id+"F41.opExtrude","SWEPT_FACE",FACE,{"disambiguationData":[OSD([sQuery(id+"F40.wireOp",EDGE,"E99.left")])]})]})})});}
            extrude(context, id + "F53", {"entities" : qUnion([Q0]), "operationType" : NewBodyOperationType.ADD, "endBound" : BoundingType.UP_TO_NEXT, "depth" : 25 * mm, "offsetDistance" : 25 * mm});
        }
        {
            var Q0;
            {var subQ0=sQuery(id+"F45.wireOp",EDGE,"E105.right");Q0=makeQuery(id+"F50.boolean.opBoolean","MERGE",FACE,{"derivedFrom":[makeQuery(id+"F46.opExtrude","SWEPT_FACE",FACE,{"disambiguationData":[OSD([subQ0])]})],"fromTools":[makeQuery(id+"F50.opExtrude","SWEPT_FACE",FACE,{"disambiguationData":[OSD([sQuery(id+"F15.wireOp",EDGE,"E55"),sQuery(id+"F45.wireOp",EDGE,"E105.top"),subQ0])]})]});}
            extrude(context, id + "F54", {"entities" : qUnion([Q0]), "operationType" : NewBodyOperationType.ADD, "depth" : 1.39 * mm, "offsetDistance" : 25 * mm});
        }
        {
            var Q0;
            {var subQ0=sQuery(id+"F40.wireOp",EDGE,"E99.right");Q0=makeQuery(id+"F50.boolean.opBoolean","MERGE",FACE,{"derivedFrom":[makeQuery(id+"F41.opExtrude","SWEPT_FACE",FACE,{"disambiguationData":[OSD([subQ0])]})],"fromTools":[makeQuery(id+"F50.opExtrude","SWEPT_FACE",FACE,{"disambiguationData":[OSD([sQuery(id+"F15.wireOp",EDGE,"E41"),sQuery(id+"F40.wireOp",EDGE,"E99.top"),subQ0])]})]});}
            extrude(context, id + "F55", {"entities" : qUnion([Q0]), "operationType" : NewBodyOperationType.ADD, "depth" : 1.39 * mm, "offsetDistance" : 25 * mm});
        }
        {
            var Q0;
            {var subQ0=sQuery(id+"F40.wireOp",EDGE,"E100.right");Q0=makeQuery(id+"F50.boolean.opBoolean","MERGE",FACE,{"derivedFrom":[makeQuery(id+"F41.opExtrude","SWEPT_FACE",FACE,{"disambiguationData":[OSD([subQ0])]})],"fromTools":[makeQuery(id+"F50.opExtrude","SWEPT_FACE",FACE,{"disambiguationData":[OSD([sQuery(id+"F15.wireOp",EDGE,"E41"),sQuery(id+"F40.wireOp",EDGE,"E100.top"),subQ0])]})]});}
            extrude(context, id + "F56", {"entities" : qUnion([Q0]), "operationType" : NewBodyOperationType.ADD, "depth" : 1.39 * mm, "offsetDistance" : 25 * mm});
        }
        {
            var Q0;
            {var subQ0=sQuery(id+"F48.wireOp",EDGE,"E106.right");Q0=makeQuery(id+"F50.boolean.opBoolean","MERGE",FACE,{"derivedFrom":[makeQuery(id+"F49.opExtrude","SWEPT_FACE",FACE,{"disambiguationData":[OSD([subQ0])]})],"fromTools":[makeQuery(id+"F50.opExtrude","SWEPT_FACE",FACE,{"disambiguationData":[OSD([sQuery(id+"F15.wireOp",EDGE,"E47.top"),sQuery(id+"F48.wireOp",EDGE,"E106.top"),subQ0])]})]});}
            extrude(context, id + "F57", {"entities" : qUnion([Q0]), "operationType" : NewBodyOperationType.ADD, "depth" : 1.39 * mm, "offsetDistance" : 25 * mm});
        }
        {
            var Q0;
            {var subQ0=sQuery(id+"F48.wireOp",EDGE,"E107.right");Q0=makeQuery(id+"F50.boolean.opBoolean","MERGE",FACE,{"derivedFrom":[makeQuery(id+"F49.opExtrude","SWEPT_FACE",FACE,{"disambiguationData":[OSD([subQ0])]})],"fromTools":[makeQuery(id+"F50.opExtrude","SWEPT_FACE",FACE,{"disambiguationData":[OSD([sQuery(id+"F15.wireOp",EDGE,"E47.top"),sQuery(id+"F48.wireOp",EDGE,"E107.top"),subQ0])]})]});}
            extrude(context, id + "F58", {"entities" : qUnion([Q0]), "operationType" : NewBodyOperationType.ADD, "depth" : 1.39 * mm, "offsetDistance" : 25 * mm});
        }
        {
            var Q0;
            {var subQ0=sQuery(id+"F15.wireOp",EDGE,"E41");Q0=makeQuery(id+"F50.boolean.opBoolean","MERGE",FACE,{"derivedFrom":[makeQuery(id+"F37.opExtrude","CAP_FACE",FACE,{"disambiguationData":[OSD([subQ0])],"isStart":false})],"fromTools":[makeQuery(id+"F50.opExtrude","SWEPT_FACE",FACE,{"disambiguationData":[OSD([subQ0])]})]});}
            extrude(context, id + "F59", {"entities" : qUnion([Q0]), "operationType" : NewBodyOperationType.ADD, "depth" : 1.39 * mm, "offsetDistance" : 25 * mm});
        }
        {
            var Q0;
            {var subQ0=sQuery(id+"F15.wireOp",EDGE,"E47.top");Q0=makeQuery(id+"F50.boolean.opBoolean","MERGE",FACE,{"derivedFrom":[makeQuery(id+"F38.opExtrude","CAP_FACE",FACE,{"disambiguationData":[OSD([subQ0])],"isStart":false})],"fromTools":[makeQuery(id+"F50.opExtrude","SWEPT_FACE",FACE,{"disambiguationData":[OSD([subQ0])]})]});}
            extrude(context, id + "F60", {"entities" : qUnion([Q0]), "operationType" : NewBodyOperationType.ADD, "depth" : 1.39 * mm, "offsetDistance" : 25 * mm});
        }
        {
            var Q0;
            {var subQ0=sQuery(id+"F15.wireOp",EDGE,"E55");var subQ2=sQuery(id+"F15.wireOp",EDGE,"E52");Q0=makeQuery(id+"F50.boolean.opBoolean","MERGE",FACE,{"derivedFrom":[makeQuery(id+"F39.boolean.opBoolean","SPLIT",FACE,{"disambiguationData":[TD([makeQuery(id+"F16.opExtrude","SWEPT_FACE",FACE,{"disambiguationData":[OSD([subQ2])]})])],"derivedFrom":makeQuery(id+"F39.opExtrude","CAP_FACE",FACE,{"disambiguationData":[OSD([subQ0])],"isStart":false})})],"fromTools":[makeQuery(id+"F50.opExtrude","SWEPT_FACE",FACE,{"disambiguationData":[OSD([subQ0])]})]});}
            extrude(context, id + "F61", {"entities" : qUnion([Q0]), "operationType" : NewBodyOperationType.ADD, "depth" : 1.39 * mm, "offsetDistance" : 25 * mm});
        }
    });
